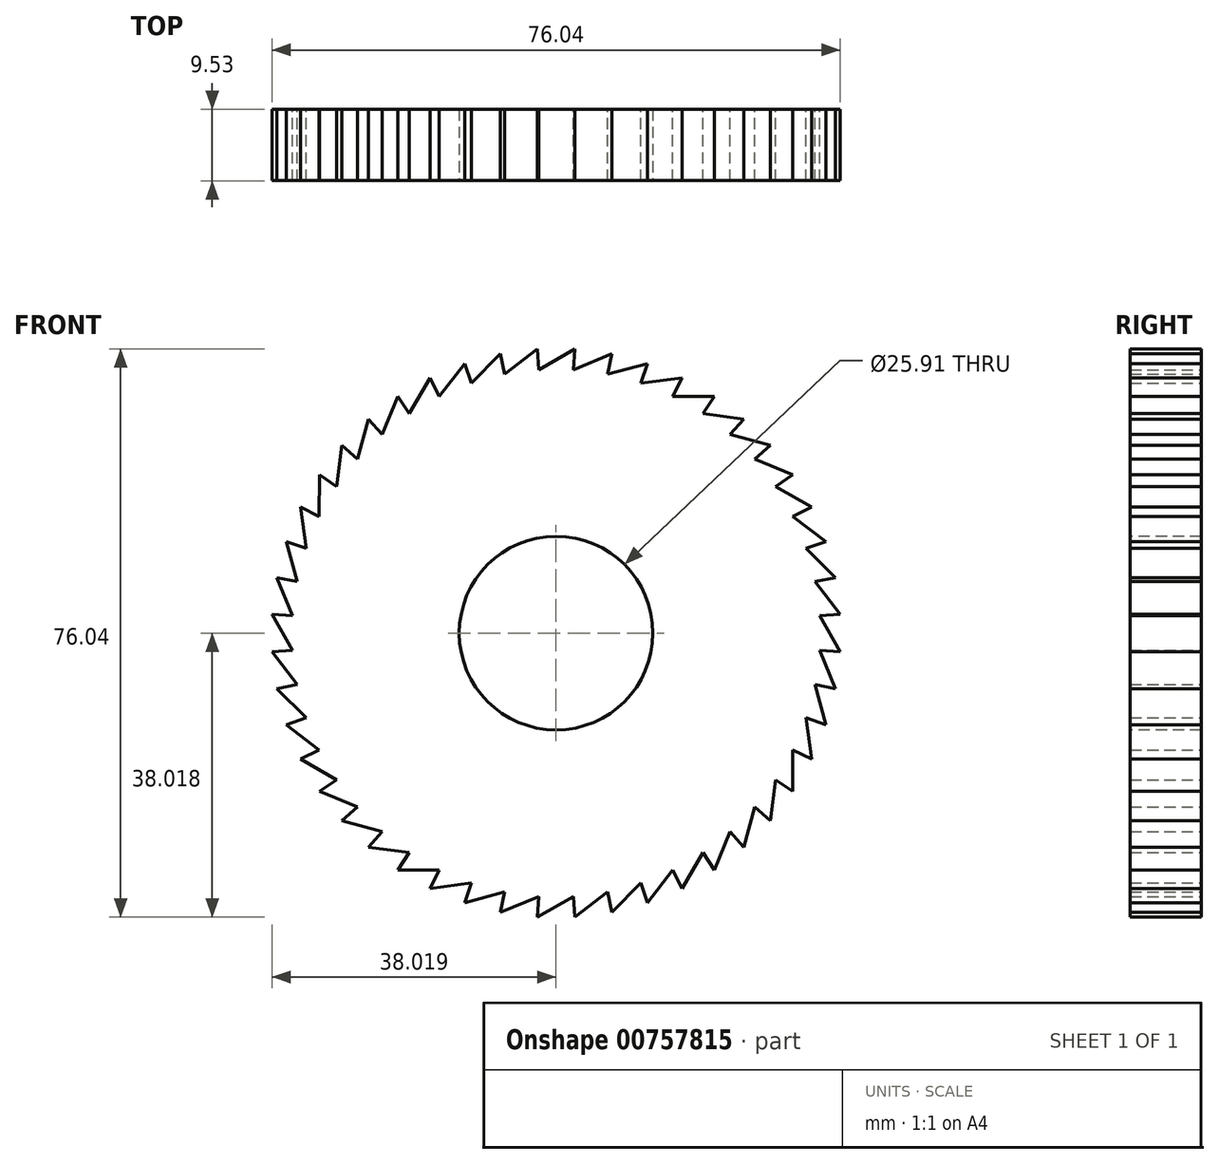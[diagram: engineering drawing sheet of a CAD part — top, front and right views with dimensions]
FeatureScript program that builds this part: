
annotation { "Feature Type Name" : "Feature", "Feature Type Description" : "" }
export const myFeature = defineFeature(function(context is Context, id is Id, definition is map)
    precondition{}
    {
        {
            var Q0;
            Q0=qCreatedBy(makeId("Front.planeOp"),FACE);
            var sketch = newSketch(context, id + "F0", { "sketchPlane" : qUnion([Q0])});
            skLineSegment(sketch, "E0", {"start": v(-136.17, -101.6) * mm, "end": v(-136.17, 101.6) * mm});
            skLineSegment(sketch, "E1", {"start": v(130.53, -101.6) * mm, "end": v(130.53, 101.6) * mm});
            skLineSegment(sketch, "E2", {"start": v(130.53, 101.6) * mm, "end": v(-136.17, 101.6) * mm});
            skLineSegment(sketch, "E3", {"start": v(-136.17, -101.6) * mm, "end": v(130.53, -101.6) * mm});
            skLineSegment(sketch, "E4", {"start": v(130.53, -82.55) * mm, "end": v(13.06, -82.55) * mm});
            skLineSegment(sketch, "E5", {"start": v(13.06, -82.55) * mm, "end": v(13.06, -101.6) * mm});
            skLineSegment(sketch, "E6", {"start": v(13.06, -90.49) * mm, "end": v(130.53, -90.49) * mm});
            skLineSegment(sketch, "E7", {"start": v(13.06, -98.43) * mm, "end": v(68.62, -98.43) * mm});
            skLineSegment(sketch, "E8", {"start": v(68.62, -98.43) * mm, "end": v(68.62, -101.6) * mm});
            skLineSegment(sketch, "E9", {"start": v(68.62, -98.43) * mm, "end": v(68.62, -90.49) * mm});
            skLineSegment(sketch, "E10", {"start": v(68.62, -90.49) * mm, "end": v(68.62, -82.55) * mm});
            skLineSegment(sketch, "E11", {"start": v(-53.64, 28.66) * mm, "end": v(-53.46, 31.43) * mm});
            skLineSegment(sketch, "E12", {"start": v(-48.52, 30.78) * mm, "end": v(-53.64, 28.66) * mm});
            skLineSegment(sketch, "E13", {"start": v(-49.06, 28.05) * mm, "end": v(-48.52, 30.78) * mm});
            skLineSegment(sketch, "E14", {"start": v(-43.7, 29.49) * mm, "end": v(-49.06, 28.05) * mm});
            skLineSegment(sketch, "E15", {"start": v(-44.6, 26.86) * mm, "end": v(-43.7, 29.49) * mm});
            skLineSegment(sketch, "E16", {"start": v(-39.1, 27.58) * mm, "end": v(-44.6, 26.86) * mm});
            skLineSegment(sketch, "E17", {"start": v(-40.33, 25.1) * mm, "end": v(-39.1, 27.58) * mm});
            skLineSegment(sketch, "E18", {"start": v(-34.78, 25.09) * mm, "end": v(-40.33, 25.1) * mm});
            skLineSegment(sketch, "E19", {"start": v(-36.33, 22.78) * mm, "end": v(-34.78, 25.09) * mm});
            skLineSegment(sketch, "E20", {"start": v(-30.83, 22.05) * mm, "end": v(-36.33, 22.78) * mm});
            skLineSegment(sketch, "E21", {"start": v(-32.66, 19.97) * mm, "end": v(-30.83, 22.05) * mm});
            skLineSegment(sketch, "E22", {"start": v(-27.3, 18.53) * mm, "end": v(-32.66, 19.97) * mm});
            skLineSegment(sketch, "E23", {"start": v(-29.4, 16.7) * mm, "end": v(-27.3, 18.53) * mm});
            skLineSegment(sketch, "E24", {"start": v(-24.27, 14.58) * mm, "end": v(-29.4, 16.7) * mm});
            skLineSegment(sketch, "E25", {"start": v(-26.58, 13.03) * mm, "end": v(-24.27, 14.58) * mm});
            skLineSegment(sketch, "E26", {"start": v(-21.78, 10.26) * mm, "end": v(-26.58, 13.03) * mm});
            skLineSegment(sketch, "E27", {"start": v(-24.27, 9.03) * mm, "end": v(-21.78, 10.26) * mm});
            skLineSegment(sketch, "E28", {"start": v(-19.87, 5.66) * mm, "end": v(-24.27, 9.03) * mm});
            skLineSegment(sketch, "E29", {"start": v(-22.5, 4.76) * mm, "end": v(-19.87, 5.66) * mm});
            skLineSegment(sketch, "E30", {"start": v(-18.58, 0.84) * mm, "end": v(-22.5, 4.76) * mm});
            skLineSegment(sketch, "E31", {"start": v(-21.3, 0.3) * mm, "end": v(-18.58, 0.84) * mm});
            skLineSegment(sketch, "E32", {"start": v(-17.93, -4.1) * mm, "end": v(-21.3, 0.3) * mm});
            skLineSegment(sketch, "E33", {"start": v(-20.7, -4.28) * mm, "end": v(-17.93, -4.1) * mm});
            skLineSegment(sketch, "E34", {"start": v(-17.93, -9.08) * mm, "end": v(-20.7, -4.28) * mm});
            skLineSegment(sketch, "E35", {"start": v(-20.7, -8.9) * mm, "end": v(-17.93, -9.08) * mm});
            skLineSegment(sketch, "E36", {"start": v(-18.58, -14.02) * mm, "end": v(-20.7, -8.9) * mm});
            skLineSegment(sketch, "E37", {"start": v(-21.3, -13.48) * mm, "end": v(-18.58, -14.02) * mm});
            skLineSegment(sketch, "E38", {"start": v(-19.87, -18.84) * mm, "end": v(-21.3, -13.48) * mm});
            skLineSegment(sketch, "E39", {"start": v(-22.5, -17.95) * mm, "end": v(-19.87, -18.84) * mm});
            skLineSegment(sketch, "E40", {"start": v(-21.78, -23.44) * mm, "end": v(-22.5, -17.95) * mm});
            skLineSegment(sketch, "E41", {"start": v(-24.27, -22.22) * mm, "end": v(-21.78, -23.44) * mm});
            skLineSegment(sketch, "E42", {"start": v(-24.27, -27.76) * mm, "end": v(-24.27, -22.22) * mm});
            skLineSegment(sketch, "E43", {"start": v(-26.58, -26.22) * mm, "end": v(-24.27, -27.76) * mm});
            skLineSegment(sketch, "E44", {"start": v(-27.3, -31.71) * mm, "end": v(-26.58, -26.22) * mm});
            skLineSegment(sketch, "E45", {"start": v(-29.4, -29.88) * mm, "end": v(-27.3, -31.71) * mm});
            skLineSegment(sketch, "E46", {"start": v(-30.83, -35.24) * mm, "end": v(-29.4, -29.88) * mm});
            skLineSegment(sketch, "E47", {"start": v(-32.66, -33.15) * mm, "end": v(-30.83, -35.24) * mm});
            skLineSegment(sketch, "E48", {"start": v(-34.78, -38.27) * mm, "end": v(-32.66, -33.15) * mm});
            skLineSegment(sketch, "E49", {"start": v(-36.33, -35.96) * mm, "end": v(-34.78, -38.27) * mm});
            skLineSegment(sketch, "E50", {"start": v(-39.1, -40.76) * mm, "end": v(-36.33, -35.96) * mm});
            skLineSegment(sketch, "E51", {"start": v(-40.33, -38.27) * mm, "end": v(-39.1, -40.76) * mm});
            skLineSegment(sketch, "E52", {"start": v(-43.7, -42.67) * mm, "end": v(-40.33, -38.27) * mm});
            skLineSegment(sketch, "E53", {"start": v(-44.6, -40.04) * mm, "end": v(-43.7, -42.67) * mm});
            skLineSegment(sketch, "E54", {"start": v(-48.52, -43.96) * mm, "end": v(-44.6, -40.04) * mm});
            skLineSegment(sketch, "E55", {"start": v(-49.06, -41.24) * mm, "end": v(-48.52, -43.96) * mm});
            skLineSegment(sketch, "E56", {"start": v(-53.46, -44.61) * mm, "end": v(-49.06, -41.24) * mm});
            skLineSegment(sketch, "E57", {"start": v(-53.64, -41.84) * mm, "end": v(-53.46, -44.61) * mm});
            skLineSegment(sketch, "E58", {"start": v(-58.44, -44.61) * mm, "end": v(-53.64, -41.84) * mm});
            skLineSegment(sketch, "E59", {"start": v(-58.26, -41.84) * mm, "end": v(-58.44, -44.61) * mm});
            skLineSegment(sketch, "E60", {"start": v(-63.38, -43.96) * mm, "end": v(-58.26, -41.84) * mm});
            skLineSegment(sketch, "E61", {"start": v(-68.2, -42.67) * mm, "end": v(-62.84, -41.24) * mm});
            skLineSegment(sketch, "E62", {"start": v(-67.3, -40.04) * mm, "end": v(-68.2, -42.67) * mm});
            skLineSegment(sketch, "E63", {"start": v(-72.8, -40.76) * mm, "end": v(-67.3, -40.04) * mm});
            skLineSegment(sketch, "E64", {"start": v(-71.57, -38.27) * mm, "end": v(-72.8, -40.76) * mm});
            skLineSegment(sketch, "E65", {"start": v(-77.12, -38.27) * mm, "end": v(-71.57, -38.27) * mm});
            skLineSegment(sketch, "E66", {"start": v(-75.58, -35.96) * mm, "end": v(-77.12, -38.27) * mm});
            skLineSegment(sketch, "E67", {"start": v(-81.07, -35.24) * mm, "end": v(-75.58, -35.96) * mm});
            skLineSegment(sketch, "E68", {"start": v(-79.24, -33.15) * mm, "end": v(-81.07, -35.24) * mm});
            skLineSegment(sketch, "E69", {"start": v(-84.6, -31.71) * mm, "end": v(-79.24, -33.15) * mm});
            skLineSegment(sketch, "E70", {"start": v(-82.5, -29.88) * mm, "end": v(-84.6, -31.71) * mm});
            skLineSegment(sketch, "E71", {"start": v(-87.63, -27.76) * mm, "end": v(-82.5, -29.88) * mm});
            skLineSegment(sketch, "E72", {"start": v(-85.32, -26.22) * mm, "end": v(-87.63, -27.76) * mm});
            skLineSegment(sketch, "E73", {"start": v(-90.12, -23.44) * mm, "end": v(-85.32, -26.22) * mm});
            skLineSegment(sketch, "E74", {"start": v(-87.63, -22.22) * mm, "end": v(-90.12, -23.44) * mm});
            skLineSegment(sketch, "E75", {"start": v(-92.03, -18.84) * mm, "end": v(-87.63, -22.22) * mm});
            skLineSegment(sketch, "E76", {"start": v(-89.4, -17.95) * mm, "end": v(-92.03, -18.84) * mm});
            skLineSegment(sketch, "E77", {"start": v(-93.32, -14.02) * mm, "end": v(-89.4, -17.95) * mm});
            skLineSegment(sketch, "E78", {"start": v(-90.6, -13.48) * mm, "end": v(-93.32, -14.02) * mm});
            skLineSegment(sketch, "E79", {"start": v(-93.97, -9.08) * mm, "end": v(-90.6, -13.48) * mm});
            skLineSegment(sketch, "E80", {"start": v(-91.2, -8.9) * mm, "end": v(-93.97, -9.08) * mm});
            skLineSegment(sketch, "E81", {"start": v(-93.97, -4.1) * mm, "end": v(-91.2, -8.9) * mm});
            skLineSegment(sketch, "E82", {"start": v(-91.2, -4.28) * mm, "end": v(-93.97, -4.1) * mm});
            skLineSegment(sketch, "E83", {"start": v(-93.32, 0.84) * mm, "end": v(-91.2, -4.28) * mm});
            skLineSegment(sketch, "E84", {"start": v(-90.6, 0.3) * mm, "end": v(-93.32, 0.84) * mm});
            skLineSegment(sketch, "E85", {"start": v(-92.03, 5.66) * mm, "end": v(-90.6, 0.3) * mm});
            skLineSegment(sketch, "E86", {"start": v(-89.4, 4.76) * mm, "end": v(-92.03, 5.66) * mm});
            skLineSegment(sketch, "E87", {"start": v(-90.12, 10.26) * mm, "end": v(-89.4, 4.76) * mm});
            skLineSegment(sketch, "E88", {"start": v(-87.63, 9.03) * mm, "end": v(-90.12, 10.26) * mm});
            skLineSegment(sketch, "E89", {"start": v(-87.63, 14.58) * mm, "end": v(-87.63, 9.03) * mm});
            skLineSegment(sketch, "E90", {"start": v(-85.32, 13.03) * mm, "end": v(-87.63, 14.58) * mm});
            skLineSegment(sketch, "E91", {"start": v(-84.6, 18.53) * mm, "end": v(-85.32, 13.03) * mm});
            skLineSegment(sketch, "E92", {"start": v(-82.5, 16.7) * mm, "end": v(-84.6, 18.53) * mm});
            skLineSegment(sketch, "E93", {"start": v(-81.07, 22.05) * mm, "end": v(-82.5, 16.7) * mm});
            skLineSegment(sketch, "E94", {"start": v(-79.24, 19.97) * mm, "end": v(-81.07, 22.05) * mm});
            skLineSegment(sketch, "E95", {"start": v(-77.12, 25.09) * mm, "end": v(-79.24, 19.97) * mm});
            skLineSegment(sketch, "E96", {"start": v(-75.58, 22.78) * mm, "end": v(-77.12, 25.09) * mm});
            skLineSegment(sketch, "E97", {"start": v(-72.8, 27.58) * mm, "end": v(-75.58, 22.78) * mm});
            skLineSegment(sketch, "E98", {"start": v(-71.57, 25.1) * mm, "end": v(-72.8, 27.58) * mm});
            skLineSegment(sketch, "E99", {"start": v(-68.2, 29.49) * mm, "end": v(-71.57, 25.1) * mm});
            skLineSegment(sketch, "E100", {"start": v(-67.3, 26.86) * mm, "end": v(-68.2, 29.49) * mm});
            skLineSegment(sketch, "E101", {"start": v(-63.38, 30.78) * mm, "end": v(-67.3, 26.86) * mm});
            skLineSegment(sketch, "E102", {"start": v(-62.84, 28.05) * mm, "end": v(-63.38, 30.78) * mm});
            skLineSegment(sketch, "E103", {"start": v(-58.44, 31.43) * mm, "end": v(-62.84, 28.05) * mm});
            skLineSegment(sketch, "E104", {"start": v(-58.26, 28.66) * mm, "end": v(-58.44, 31.43) * mm});
            skLineSegment(sketch, "E105", {"start": v(-53.46, 31.43) * mm, "end": v(-58.26, 28.66) * mm});
            skCircle(sketch, "E106", {"center": v(-55.95, -6.6) * mm, "radius": 8.9 * mm});
            skLineSegment(sketch, "E107", {"start": v(-62.84, -41.24) * mm, "end": v(-63.38, -43.96) * mm});
            skCircle(sketch, "E108", {"center": v(-55.95, -6.6) * mm, "radius": 8.73 * mm});
            skLineSegment(sketch, "E109", {"start": v(-46.26, 37.72) * mm, "end": v(-19.3, 38.64) * mm});
            skLineSegment(sketch, "E110", {"start": v(-52.38, 30.8) * mm, "end": v(-52.4, 31.16) * mm});
            skLineSegment(sketch, "E111", {"start": v(-52.38, 30.8) * mm, "end": v(-51.42, 30.84) * mm});
            skLineSegment(sketch, "E112", {"start": v(-40.64, 31.2) * mm, "end": v(-19.77, 25.99) * mm});
            skArc(sketch, "E113", {"start": v(-46.26, 37.72) * mm, "mid": v(-50.69, 35.71) * mm, "end": v(-52.4, 31.16) * mm});
            skArc(sketch, "E114", {"start": v(-40.64, 31.2) * mm, "mid": v(-46.11, 33.48) * mm, "end": v(-51.42, 30.84) * mm});
            skArc(sketch, "E115", {"start": v(-19.77, 25.99) * mm, "mid": v(-12.73, 32.06) * mm, "end": v(-19.3, 38.64) * mm});
            skCircle(sketch, "E116", {"center": v(-19.07, 32.3) * mm, "radius": 3.19 * mm});
            skLineSegment(sketch, "E117", {"start": v(58.58, 2.14) * mm, "end": v(67.76, 2.14) * mm});
            skLineSegment(sketch, "E118", {"start": v(67.76, 2.14) * mm, "end": v(67.93, 2.31) * mm});
            skLineSegment(sketch, "E119", {"start": v(58.58, 2.14) * mm, "end": v(58.4, 2.31) * mm});
            skLineSegment(sketch, "E120", {"start": v(58.4, -15.5) * mm, "end": v(58.58, -15.32) * mm});
            skLineSegment(sketch, "E121", {"start": v(58.58, -15.32) * mm, "end": v(67.76, -15.32) * mm});
            skLineSegment(sketch, "E122", {"start": v(67.76, -15.32) * mm, "end": v(67.93, -15.5) * mm});
            skLineSegment(sketch, "E123", {"start": v(67.93, -4.28) * mm, "end": v(58.4, -4.28) * mm});
            skLineSegment(sketch, "E124", {"start": v(58.4, -9.08) * mm, "end": v(58.4, -4.28) * mm});
            skLineSegment(sketch, "E125", {"start": v(67.93, -9.08) * mm, "end": v(58.4, -9.08) * mm});
            skLineSegment(sketch, "E126", {"start": v(67.93, -9.08) * mm, "end": v(67.93, -4.28) * mm});
            skLineSegment(sketch, "E127", {"start": v(67.93, -4.1) * mm, "end": v(58.4, -4.1) * mm});
            skLineSegment(sketch, "E128", {"start": v(58.4, -4.28) * mm, "end": v(58.4, -4.1) * mm});
            skLineSegment(sketch, "E129", {"start": v(67.93, -4.28) * mm, "end": v(67.93, -4.1) * mm});
            skLineSegment(sketch, "E130", {"start": v(67.93, 0.3) * mm, "end": v(58.4, 0.3) * mm});
            skLineSegment(sketch, "E131", {"start": v(58.4, -4.1) * mm, "end": v(58.4, 0.3) * mm});
            skLineSegment(sketch, "E132", {"start": v(67.93, -4.1) * mm, "end": v(67.93, 0.3) * mm});
            skLineSegment(sketch, "E133", {"start": v(67.93, -14.02) * mm, "end": v(58.4, -14.02) * mm});
            skLineSegment(sketch, "E134", {"start": v(58.4, -14.02) * mm, "end": v(58.4, -9.08) * mm});
            skLineSegment(sketch, "E135", {"start": v(67.93, -14.02) * mm, "end": v(67.93, -9.08) * mm});
            skLineSegment(sketch, "E136", {"start": v(67.93, 4.76) * mm, "end": v(58.4, 4.76) * mm});
            skLineSegment(sketch, "E137", {"start": v(67.93, 0.84) * mm, "end": v(58.4, 0.84) * mm});
            skLineSegment(sketch, "E138", {"start": v(58.4, 0.84) * mm, "end": v(58.4, 4.76) * mm});
            skLineSegment(sketch, "E139", {"start": v(67.93, 0.84) * mm, "end": v(67.93, 4.76) * mm});
            skLineSegment(sketch, "E140", {"start": v(58.4, 0.3) * mm, "end": v(58.4, 0.84) * mm});
            skLineSegment(sketch, "E141", {"start": v(67.93, 0.3) * mm, "end": v(67.93, 0.84) * mm});
            skLineSegment(sketch, "E142", {"start": v(67.93, -18.84) * mm, "end": v(58.4, -18.84) * mm});
            skLineSegment(sketch, "E143", {"start": v(58.4, -18.84) * mm, "end": v(58.4, -14.02) * mm});
            skLineSegment(sketch, "E144", {"start": v(67.93, -18.84) * mm, "end": v(67.93, -14.02) * mm});
            skLineSegment(sketch, "E145", {"start": v(67.93, 9.03) * mm, "end": v(58.4, 9.03) * mm});
            skLineSegment(sketch, "E146", {"start": v(67.93, 5.66) * mm, "end": v(58.4, 5.66) * mm});
            skLineSegment(sketch, "E147", {"start": v(58.4, 5.66) * mm, "end": v(58.4, 9.03) * mm});
            skLineSegment(sketch, "E148", {"start": v(67.93, 5.66) * mm, "end": v(67.93, 9.03) * mm});
            skLineSegment(sketch, "E149", {"start": v(58.4, 4.76) * mm, "end": v(58.4, 5.66) * mm});
            skLineSegment(sketch, "E150", {"start": v(67.93, 4.76) * mm, "end": v(67.93, 5.66) * mm});
            skLineSegment(sketch, "E151", {"start": v(67.93, -23.44) * mm, "end": v(58.4, -23.44) * mm});
            skLineSegment(sketch, "E152", {"start": v(58.4, -23.44) * mm, "end": v(58.4, -18.84) * mm});
            skLineSegment(sketch, "E153", {"start": v(67.93, -23.44) * mm, "end": v(67.93, -18.84) * mm});
            skLineSegment(sketch, "E154", {"start": v(67.93, 10.26) * mm, "end": v(58.4, 10.26) * mm});
            skLineSegment(sketch, "E155", {"start": v(58.4, 9.03) * mm, "end": v(58.4, 10.26) * mm});
            skLineSegment(sketch, "E156", {"start": v(67.93, 9.03) * mm, "end": v(67.93, 10.26) * mm});
            skLineSegment(sketch, "E157", {"start": v(67.93, 13.03) * mm, "end": v(58.4, 13.03) * mm});
            skLineSegment(sketch, "E158", {"start": v(58.4, 10.26) * mm, "end": v(58.4, 13.03) * mm});
            skLineSegment(sketch, "E159", {"start": v(67.93, 10.26) * mm, "end": v(67.93, 13.03) * mm});
            skLineSegment(sketch, "E160", {"start": v(67.93, -27.76) * mm, "end": v(58.4, -27.76) * mm});
            skLineSegment(sketch, "E161", {"start": v(58.4, -27.76) * mm, "end": v(58.4, -23.44) * mm});
            skLineSegment(sketch, "E162", {"start": v(67.93, -27.76) * mm, "end": v(67.93, -23.44) * mm});
            skLineSegment(sketch, "E163", {"start": v(67.93, 16.7) * mm, "end": v(58.4, 16.7) * mm});
            skLineSegment(sketch, "E164", {"start": v(67.93, 14.58) * mm, "end": v(58.4, 14.58) * mm});
            skLineSegment(sketch, "E165", {"start": v(58.4, 14.58) * mm, "end": v(58.4, 16.7) * mm});
            skLineSegment(sketch, "E166", {"start": v(67.93, 14.58) * mm, "end": v(67.93, 16.7) * mm});
            skLineSegment(sketch, "E167", {"start": v(58.4, 13.03) * mm, "end": v(58.4, 14.58) * mm});
            skLineSegment(sketch, "E168", {"start": v(67.93, 13.03) * mm, "end": v(67.93, 14.58) * mm});
            skLineSegment(sketch, "E169", {"start": v(67.93, -31.71) * mm, "end": v(58.4, -31.71) * mm});
            skLineSegment(sketch, "E170", {"start": v(58.4, -31.71) * mm, "end": v(58.4, -27.76) * mm});
            skLineSegment(sketch, "E171", {"start": v(67.93, -31.71) * mm, "end": v(67.93, -27.76) * mm});
            skLineSegment(sketch, "E172", {"start": v(67.93, 19.97) * mm, "end": v(58.4, 19.97) * mm});
            skLineSegment(sketch, "E173", {"start": v(67.93, 18.53) * mm, "end": v(58.4, 18.53) * mm});
            skLineSegment(sketch, "E174", {"start": v(58.4, 18.53) * mm, "end": v(58.4, 19.97) * mm});
            skLineSegment(sketch, "E175", {"start": v(67.93, 18.53) * mm, "end": v(67.93, 19.97) * mm});
            skLineSegment(sketch, "E176", {"start": v(58.4, 16.7) * mm, "end": v(58.4, 18.53) * mm});
            skLineSegment(sketch, "E177", {"start": v(67.93, 16.7) * mm, "end": v(67.93, 18.53) * mm});
            skLineSegment(sketch, "E178", {"start": v(67.93, -35.24) * mm, "end": v(58.4, -35.24) * mm});
            skLineSegment(sketch, "E179", {"start": v(58.4, -35.24) * mm, "end": v(58.4, -31.71) * mm});
            skLineSegment(sketch, "E180", {"start": v(67.93, -35.24) * mm, "end": v(67.93, -31.71) * mm});
            skLineSegment(sketch, "E181", {"start": v(67.93, 22.78) * mm, "end": v(58.4, 22.78) * mm});
            skLineSegment(sketch, "E182", {"start": v(67.93, 22.05) * mm, "end": v(58.4, 22.05) * mm});
            skLineSegment(sketch, "E183", {"start": v(58.4, 22.05) * mm, "end": v(58.4, 22.78) * mm});
            skLineSegment(sketch, "E184", {"start": v(67.93, 22.05) * mm, "end": v(67.93, 22.78) * mm});
            skLineSegment(sketch, "E185", {"start": v(58.4, 19.97) * mm, "end": v(58.4, 22.05) * mm});
            skLineSegment(sketch, "E186", {"start": v(67.93, 19.97) * mm, "end": v(67.93, 22.05) * mm});
            skLineSegment(sketch, "E187", {"start": v(67.93, -38.27) * mm, "end": v(58.4, -38.27) * mm});
            skLineSegment(sketch, "E188", {"start": v(58.4, -38.27) * mm, "end": v(58.4, -35.24) * mm});
            skLineSegment(sketch, "E189", {"start": v(67.93, -38.27) * mm, "end": v(67.93, -35.24) * mm});
            skLineSegment(sketch, "E190", {"start": v(67.93, 25.1) * mm, "end": v(58.4, 25.1) * mm});
            skLineSegment(sketch, "E191", {"start": v(67.93, 25.09) * mm, "end": v(58.4, 25.09) * mm});
            skLineSegment(sketch, "E192", {"start": v(58.4, 25.09) * mm, "end": v(58.4, 25.1) * mm});
            skLineSegment(sketch, "E193", {"start": v(67.93, 25.09) * mm, "end": v(67.93, 25.1) * mm});
            skLineSegment(sketch, "E194", {"start": v(58.4, 22.78) * mm, "end": v(58.4, 25.09) * mm});
            skLineSegment(sketch, "E195", {"start": v(67.93, 22.78) * mm, "end": v(67.93, 25.09) * mm});
            skLineSegment(sketch, "E196", {"start": v(67.93, -40.76) * mm, "end": v(58.4, -40.76) * mm});
            skLineSegment(sketch, "E197", {"start": v(58.4, -40.76) * mm, "end": v(58.4, -38.27) * mm});
            skLineSegment(sketch, "E198", {"start": v(67.93, -40.76) * mm, "end": v(67.93, -38.27) * mm});
            skLineSegment(sketch, "E199", {"start": v(67.93, 27.58) * mm, "end": v(58.4, 27.58) * mm});
            skLineSegment(sketch, "E200", {"start": v(58.4, 25.1) * mm, "end": v(58.4, 27.58) * mm});
            skLineSegment(sketch, "E201", {"start": v(67.93, 25.1) * mm, "end": v(67.93, 27.58) * mm});
            skLineSegment(sketch, "E202", {"start": v(67.93, -42.67) * mm, "end": v(58.4, -42.67) * mm});
            skLineSegment(sketch, "E203", {"start": v(58.4, -42.67) * mm, "end": v(58.4, -40.76) * mm});
            skLineSegment(sketch, "E204", {"start": v(67.93, -42.67) * mm, "end": v(67.93, -40.76) * mm});
            skLineSegment(sketch, "E205", {"start": v(67.93, 29.49) * mm, "end": v(58.4, 29.49) * mm});
            skLineSegment(sketch, "E206", {"start": v(58.4, 27.58) * mm, "end": v(58.4, 29.49) * mm});
            skLineSegment(sketch, "E207", {"start": v(67.93, 27.58) * mm, "end": v(67.93, 29.49) * mm});
            skLineSegment(sketch, "E208", {"start": v(67.93, -43.96) * mm, "end": v(58.4, -43.96) * mm});
            skLineSegment(sketch, "E209", {"start": v(58.4, -43.96) * mm, "end": v(58.4, -42.67) * mm});
            skLineSegment(sketch, "E210", {"start": v(67.93, -43.96) * mm, "end": v(67.93, -42.67) * mm});
            skLineSegment(sketch, "E211", {"start": v(67.93, 30.78) * mm, "end": v(58.4, 30.78) * mm});
            skLineSegment(sketch, "E212", {"start": v(58.4, 29.49) * mm, "end": v(58.4, 30.78) * mm});
            skLineSegment(sketch, "E213", {"start": v(67.93, 29.49) * mm, "end": v(67.93, 30.78) * mm});
            skLineSegment(sketch, "E214", {"start": v(67.93, -44.61) * mm, "end": v(58.4, -44.61) * mm});
            skLineSegment(sketch, "E215", {"start": v(58.4, -44.61) * mm, "end": v(58.4, -43.96) * mm});
            skLineSegment(sketch, "E216", {"start": v(67.93, -44.61) * mm, "end": v(67.93, -43.96) * mm});
            skLineSegment(sketch, "E217", {"start": v(67.93, 31.43) * mm, "end": v(58.4, 31.43) * mm});
            skLineSegment(sketch, "E218", {"start": v(58.4, 30.78) * mm, "end": v(58.4, 31.43) * mm});
            skLineSegment(sketch, "E219", {"start": v(67.93, 30.78) * mm, "end": v(67.93, 31.43) * mm});
            skLineSegment(sketch, "E220", {"start": v(104.22, 94.72) * mm, "end": v(104.29, 96.04) * mm});
            skLineSegment(sketch, "E221", {"start": v(106.03, 95.26) * mm, "end": v(104.22, 94.72) * mm});
            skLineSegment(sketch, "E222", {"start": v(105.84, 94) * mm, "end": v(106.03, 95.26) * mm});
            skLineSegment(sketch, "E223", {"start": v(107.73, 94.18) * mm, "end": v(105.84, 94) * mm});
            skLineSegment(sketch, "E224", {"start": v(107.42, 93) * mm, "end": v(107.73, 94.18) * mm});
            skLineSegment(sketch, "E225", {"start": v(109.36, 92.83) * mm, "end": v(107.42, 93) * mm});
            skLineSegment(sketch, "E226", {"start": v(108.93, 91.74) * mm, "end": v(109.36, 92.83) * mm});
            skLineSegment(sketch, "E227", {"start": v(110.89, 91.22) * mm, "end": v(108.93, 91.74) * mm});
            skLineSegment(sketch, "E228", {"start": v(110.34, 90.25) * mm, "end": v(110.89, 91.22) * mm});
            skLineSegment(sketch, "E229", {"start": v(112.29, 89.38) * mm, "end": v(110.34, 90.25) * mm});
            skLineSegment(sketch, "E230", {"start": v(111.64, 88.55) * mm, "end": v(112.29, 89.38) * mm});
            skLineSegment(sketch, "E231", {"start": v(113.53, 87.35) * mm, "end": v(111.64, 88.55) * mm});
            skLineSegment(sketch, "E232", {"start": v(112.8, 86.67) * mm, "end": v(113.53, 87.35) * mm});
            skLineSegment(sketch, "E233", {"start": v(114.6, 85.16) * mm, "end": v(112.8, 86.67) * mm});
            skLineSegment(sketch, "E234", {"start": v(113.79, 84.63) * mm, "end": v(114.6, 85.16) * mm});
            skLineSegment(sketch, "E235", {"start": v(115.49, 82.84) * mm, "end": v(113.79, 84.63) * mm});
            skLineSegment(sketch, "E236", {"start": v(114.6, 82.49) * mm, "end": v(115.49, 82.84) * mm});
            skLineSegment(sketch, "E237", {"start": v(116.16, 80.44) * mm, "end": v(114.6, 82.49) * mm});
            skLineSegment(sketch, "E238", {"start": v(115.23, 80.26) * mm, "end": v(116.16, 80.44) * mm});
            skLineSegment(sketch, "E239", {"start": v(116.62, 78) * mm, "end": v(115.23, 80.26) * mm});
            skLineSegment(sketch, "E240", {"start": v(115.65, 78) * mm, "end": v(116.62, 78) * mm});
            skLineSegment(sketch, "E241", {"start": v(116.85, 75.56) * mm, "end": v(115.65, 78) * mm});
            skLineSegment(sketch, "E242", {"start": v(115.87, 75.74) * mm, "end": v(116.85, 75.56) * mm});
            skLineSegment(sketch, "E243", {"start": v(116.85, 73.16) * mm, "end": v(115.87, 75.74) * mm});
            skLineSegment(sketch, "E244", {"start": v(115.87, 73.5) * mm, "end": v(116.85, 73.16) * mm});
            skLineSegment(sketch, "E245", {"start": v(116.62, 70.84) * mm, "end": v(115.87, 73.5) * mm});
            skLineSegment(sketch, "E246", {"start": v(115.65, 71.36) * mm, "end": v(116.62, 70.84) * mm});
            skLineSegment(sketch, "E247", {"start": v(116.16, 68.64) * mm, "end": v(115.65, 71.36) * mm});
            skLineSegment(sketch, "E248", {"start": v(115.23, 69.32) * mm, "end": v(116.16, 68.64) * mm});
            skLineSegment(sketch, "E249", {"start": v(115.49, 66.6) * mm, "end": v(115.23, 69.32) * mm});
            skLineSegment(sketch, "E250", {"start": v(114.6, 67.43) * mm, "end": v(115.49, 66.6) * mm});
            skLineSegment(sketch, "E251", {"start": v(114.6, 64.76) * mm, "end": v(114.6, 67.43) * mm});
            skLineSegment(sketch, "E252", {"start": v(113.79, 65.73) * mm, "end": v(114.6, 64.76) * mm});
            skLineSegment(sketch, "E253", {"start": v(113.53, 63.15) * mm, "end": v(113.79, 65.73) * mm});
            skLineSegment(sketch, "E254", {"start": v(112.8, 64.23) * mm, "end": v(113.53, 63.15) * mm});
            skLineSegment(sketch, "E255", {"start": v(112.29, 61.78) * mm, "end": v(112.8, 64.23) * mm});
            skLineSegment(sketch, "E256", {"start": v(111.64, 62.96) * mm, "end": v(112.29, 61.78) * mm});
            skLineSegment(sketch, "E257", {"start": v(110.89, 60.7) * mm, "end": v(111.64, 62.96) * mm});
            skLineSegment(sketch, "E258", {"start": v(110.34, 61.95) * mm, "end": v(110.89, 60.7) * mm});
            skLineSegment(sketch, "E259", {"start": v(109.36, 59.9) * mm, "end": v(110.34, 61.95) * mm});
            skLineSegment(sketch, "E260", {"start": v(108.93, 61.22) * mm, "end": v(109.36, 59.9) * mm});
            skLineSegment(sketch, "E261", {"start": v(107.73, 59.42) * mm, "end": v(108.93, 61.22) * mm});
            skLineSegment(sketch, "E262", {"start": v(107.42, 60.77) * mm, "end": v(107.73, 59.42) * mm});
            skLineSegment(sketch, "E263", {"start": v(106.03, 59.26) * mm, "end": v(107.42, 60.77) * mm});
            skLineSegment(sketch, "E264", {"start": v(105.84, 60.62) * mm, "end": v(106.03, 59.26) * mm});
            skLineSegment(sketch, "E265", {"start": v(104.29, 59.41) * mm, "end": v(105.84, 60.62) * mm});
            skLineSegment(sketch, "E266", {"start": v(104.22, 60.76) * mm, "end": v(104.29, 59.41) * mm});
            skLineSegment(sketch, "E267", {"start": v(102.52, 59.88) * mm, "end": v(104.22, 60.76) * mm});
            skLineSegment(sketch, "E268", {"start": v(102.59, 61.2) * mm, "end": v(102.52, 59.88) * mm});
            skLineSegment(sketch, "E269", {"start": v(100.78, 60.66) * mm, "end": v(102.59, 61.2) * mm});
            skLineSegment(sketch, "E270", {"start": v(100.97, 61.92) * mm, "end": v(100.78, 60.66) * mm});
            skLineSegment(sketch, "E271", {"start": v(99.07, 61.74) * mm, "end": v(100.97, 61.92) * mm});
            skLineSegment(sketch, "E272", {"start": v(99.4, 62.92) * mm, "end": v(99.07, 61.74) * mm});
            skLineSegment(sketch, "E273", {"start": v(97.45, 63.1) * mm, "end": v(99.4, 62.92) * mm});
            skLineSegment(sketch, "E274", {"start": v(97.88, 64.18) * mm, "end": v(97.45, 63.1) * mm});
            skLineSegment(sketch, "E275", {"start": v(95.92, 64.7) * mm, "end": v(97.88, 64.18) * mm});
            skLineSegment(sketch, "E276", {"start": v(96.47, 65.67) * mm, "end": v(95.92, 64.7) * mm});
            skLineSegment(sketch, "E277", {"start": v(94.52, 66.54) * mm, "end": v(96.47, 65.67) * mm});
            skLineSegment(sketch, "E278", {"start": v(95.17, 67.37) * mm, "end": v(94.52, 66.54) * mm});
            skLineSegment(sketch, "E279", {"start": v(93.28, 68.57) * mm, "end": v(95.17, 67.37) * mm});
            skLineSegment(sketch, "E280", {"start": v(94.01, 69.26) * mm, "end": v(93.28, 68.57) * mm});
            skLineSegment(sketch, "E281", {"start": v(92.2, 70.77) * mm, "end": v(94.01, 69.26) * mm});
            skLineSegment(sketch, "E282", {"start": v(93.02, 71.29) * mm, "end": v(92.2, 70.77) * mm});
            skLineSegment(sketch, "E283", {"start": v(91.32, 73.08) * mm, "end": v(93.02, 71.29) * mm});
            skLineSegment(sketch, "E284", {"start": v(92.2, 73.44) * mm, "end": v(91.32, 73.08) * mm});
            skLineSegment(sketch, "E285", {"start": v(90.65, 75.48) * mm, "end": v(92.2, 73.44) * mm});
            skLineSegment(sketch, "E286", {"start": v(91.58, 75.66) * mm, "end": v(90.65, 75.48) * mm});
            skLineSegment(sketch, "E287", {"start": v(90.2, 77.92) * mm, "end": v(91.58, 75.66) * mm});
            skLineSegment(sketch, "E288", {"start": v(91.16, 77.92) * mm, "end": v(90.2, 77.92) * mm});
            skLineSegment(sketch, "E289", {"start": v(89.96, 80.36) * mm, "end": v(91.16, 77.92) * mm});
            skLineSegment(sketch, "E290", {"start": v(90.94, 80.19) * mm, "end": v(89.96, 80.36) * mm});
            skLineSegment(sketch, "E291", {"start": v(89.96, 82.76) * mm, "end": v(90.94, 80.19) * mm});
            skLineSegment(sketch, "E292", {"start": v(90.94, 82.41) * mm, "end": v(89.96, 82.76) * mm});
            skLineSegment(sketch, "E293", {"start": v(90.2, 85.08) * mm, "end": v(90.94, 82.41) * mm});
            skLineSegment(sketch, "E294", {"start": v(91.16, 84.56) * mm, "end": v(90.2, 85.08) * mm});
            skLineSegment(sketch, "E295", {"start": v(90.65, 87.28) * mm, "end": v(91.16, 84.56) * mm});
            skLineSegment(sketch, "E296", {"start": v(91.58, 86.6) * mm, "end": v(90.65, 87.28) * mm});
            skLineSegment(sketch, "E297", {"start": v(91.32, 89.32) * mm, "end": v(91.58, 86.6) * mm});
            skLineSegment(sketch, "E298", {"start": v(92.2, 88.49) * mm, "end": v(91.32, 89.32) * mm});
            skLineSegment(sketch, "E299", {"start": v(92.2, 91.16) * mm, "end": v(92.2, 88.49) * mm});
            skLineSegment(sketch, "E300", {"start": v(93.02, 90.2) * mm, "end": v(92.2, 91.16) * mm});
            skLineSegment(sketch, "E301", {"start": v(93.28, 92.78) * mm, "end": v(93.02, 90.2) * mm});
            skLineSegment(sketch, "E302", {"start": v(94.01, 91.7) * mm, "end": v(93.28, 92.78) * mm});
            skLineSegment(sketch, "E303", {"start": v(94.52, 94.14) * mm, "end": v(94.01, 91.7) * mm});
            skLineSegment(sketch, "E304", {"start": v(95.17, 92.96) * mm, "end": v(94.52, 94.14) * mm});
            skLineSegment(sketch, "E305", {"start": v(95.92, 95.23) * mm, "end": v(95.17, 92.96) * mm});
            skLineSegment(sketch, "E306", {"start": v(96.47, 93.97) * mm, "end": v(95.92, 95.23) * mm});
            skLineSegment(sketch, "E307", {"start": v(97.45, 96.02) * mm, "end": v(96.47, 93.97) * mm});
            skLineSegment(sketch, "E308", {"start": v(97.88, 94.7) * mm, "end": v(97.45, 96.02) * mm});
            skLineSegment(sketch, "E309", {"start": v(99.07, 96.5) * mm, "end": v(97.88, 94.7) * mm});
            skLineSegment(sketch, "E310", {"start": v(99.4, 95.15) * mm, "end": v(99.07, 96.5) * mm});
            skLineSegment(sketch, "E311", {"start": v(100.78, 96.67) * mm, "end": v(99.4, 95.15) * mm});
            skLineSegment(sketch, "E312", {"start": v(100.97, 95.3) * mm, "end": v(100.78, 96.67) * mm});
            skLineSegment(sketch, "E313", {"start": v(102.52, 96.51) * mm, "end": v(100.97, 95.3) * mm});
            skLineSegment(sketch, "E314", {"start": v(102.59, 95.16) * mm, "end": v(102.52, 96.51) * mm});
            skLineSegment(sketch, "E315", {"start": v(104.29, 96.04) * mm, "end": v(102.59, 95.16) * mm});
            skLineSegment(sketch, "E316", {"start": v(106.55, 77.12) * mm, "end": v(106.55, 77) * mm});
            skLineSegment(sketch, "E317", {"start": v(106.55, 77) * mm, "end": v(106.55, 76.9) * mm});
            skLineSegment(sketch, "E318", {"start": v(106.55, 76.9) * mm, "end": v(106.54, 76.78) * mm});
            skLineSegment(sketch, "E319", {"start": v(106.54, 76.78) * mm, "end": v(106.54, 76.67) * mm});
            skLineSegment(sketch, "E320", {"start": v(106.54, 76.67) * mm, "end": v(106.53, 76.57) * mm});
            skLineSegment(sketch, "E321", {"start": v(106.53, 76.57) * mm, "end": v(106.51, 76.46) * mm});
            skLineSegment(sketch, "E322", {"start": v(106.51, 76.46) * mm, "end": v(106.5, 76.35) * mm});
            skLineSegment(sketch, "E323", {"start": v(106.5, 76.35) * mm, "end": v(106.48, 76.24) * mm});
            skLineSegment(sketch, "E324", {"start": v(106.48, 76.24) * mm, "end": v(106.47, 76.14) * mm});
            skLineSegment(sketch, "E325", {"start": v(106.47, 76.14) * mm, "end": v(106.45, 76.04) * mm});
            skLineSegment(sketch, "E326", {"start": v(106.45, 76.04) * mm, "end": v(106.42, 75.93) * mm});
            skLineSegment(sketch, "E327", {"start": v(106.42, 75.93) * mm, "end": v(106.4, 75.83) * mm});
            skLineSegment(sketch, "E328", {"start": v(106.4, 75.83) * mm, "end": v(106.37, 75.73) * mm});
            skLineSegment(sketch, "E329", {"start": v(106.37, 75.73) * mm, "end": v(106.34, 75.64) * mm});
            skLineSegment(sketch, "E330", {"start": v(106.34, 75.64) * mm, "end": v(106.31, 75.54) * mm});
            skLineSegment(sketch, "E331", {"start": v(106.31, 75.54) * mm, "end": v(106.28, 75.45) * mm});
            skLineSegment(sketch, "E332", {"start": v(106.28, 75.45) * mm, "end": v(106.25, 75.35) * mm});
            skLineSegment(sketch, "E333", {"start": v(106.25, 75.35) * mm, "end": v(106.21, 75.26) * mm});
            skLineSegment(sketch, "E334", {"start": v(106.21, 75.26) * mm, "end": v(106.17, 75.17) * mm});
            skLineSegment(sketch, "E335", {"start": v(106.17, 75.17) * mm, "end": v(106.13, 75.09) * mm});
            skLineSegment(sketch, "E336", {"start": v(106.13, 75.09) * mm, "end": v(106.09, 75) * mm});
            skLineSegment(sketch, "E337", {"start": v(106.09, 75) * mm, "end": v(106.05, 74.92) * mm});
            skLineSegment(sketch, "E338", {"start": v(106.05, 74.92) * mm, "end": v(106, 74.84) * mm});
            skLineSegment(sketch, "E339", {"start": v(106, 74.84) * mm, "end": v(105.95, 74.76) * mm});
            skLineSegment(sketch, "E340", {"start": v(105.95, 74.76) * mm, "end": v(105.9, 74.68) * mm});
            skLineSegment(sketch, "E341", {"start": v(105.9, 74.68) * mm, "end": v(105.85, 74.6) * mm});
            skLineSegment(sketch, "E342", {"start": v(105.85, 74.6) * mm, "end": v(105.8, 74.53) * mm});
            skLineSegment(sketch, "E343", {"start": v(105.8, 74.53) * mm, "end": v(105.74, 74.46) * mm});
            skLineSegment(sketch, "E344", {"start": v(105.74, 74.46) * mm, "end": v(105.69, 74.4) * mm});
            skLineSegment(sketch, "E345", {"start": v(105.69, 74.4) * mm, "end": v(105.63, 74.33) * mm});
            skLineSegment(sketch, "E346", {"start": v(105.63, 74.33) * mm, "end": v(105.57, 74.27) * mm});
            skLineSegment(sketch, "E347", {"start": v(105.57, 74.27) * mm, "end": v(105.51, 74.2) * mm});
            skLineSegment(sketch, "E348", {"start": v(105.51, 74.2) * mm, "end": v(105.45, 74.15) * mm});
            skLineSegment(sketch, "E349", {"start": v(105.45, 74.15) * mm, "end": v(105.39, 74.1) * mm});
            skLineSegment(sketch, "E350", {"start": v(105.39, 74.1) * mm, "end": v(105.32, 74.04) * mm});
            skLineSegment(sketch, "E351", {"start": v(105.32, 74.04) * mm, "end": v(105.26, 74) * mm});
            skLineSegment(sketch, "E352", {"start": v(105.26, 74) * mm, "end": v(105.19, 73.95) * mm});
            skLineSegment(sketch, "E353", {"start": v(105.19, 73.95) * mm, "end": v(105.12, 73.9) * mm});
            skLineSegment(sketch, "E354", {"start": v(105.12, 73.9) * mm, "end": v(105.05, 73.86) * mm});
            skLineSegment(sketch, "E355", {"start": v(105.05, 73.86) * mm, "end": v(104.98, 73.82) * mm});
            skLineSegment(sketch, "E356", {"start": v(104.98, 73.82) * mm, "end": v(104.9, 73.79) * mm});
            skLineSegment(sketch, "E357", {"start": v(104.9, 73.79) * mm, "end": v(104.83, 73.76) * mm});
            skLineSegment(sketch, "E358", {"start": v(104.83, 73.76) * mm, "end": v(104.76, 73.73) * mm});
            skLineSegment(sketch, "E359", {"start": v(104.76, 73.73) * mm, "end": v(104.69, 73.7) * mm});
            skLineSegment(sketch, "E360", {"start": v(104.69, 73.7) * mm, "end": v(104.6, 73.68) * mm});
            skLineSegment(sketch, "E361", {"start": v(104.6, 73.68) * mm, "end": v(104.53, 73.65) * mm});
            skLineSegment(sketch, "E362", {"start": v(104.53, 73.65) * mm, "end": v(104.46, 73.64) * mm});
            skLineSegment(sketch, "E363", {"start": v(104.46, 73.64) * mm, "end": v(104.38, 73.62) * mm});
            skLineSegment(sketch, "E364", {"start": v(104.38, 73.62) * mm, "end": v(104.3, 73.6) * mm});
            skLineSegment(sketch, "E365", {"start": v(104.3, 73.6) * mm, "end": v(104.22, 73.6) * mm});
            skLineSegment(sketch, "E366", {"start": v(104.22, 73.6) * mm, "end": v(104.14, 73.6) * mm});
            skLineSegment(sketch, "E367", {"start": v(104.14, 73.6) * mm, "end": v(104.06, 73.59) * mm});
            skLineSegment(sketch, "E368", {"start": v(104.06, 73.59) * mm, "end": v(103.98, 73.59) * mm});
            skLineSegment(sketch, "E369", {"start": v(103.98, 73.59) * mm, "end": v(103.9, 73.6) * mm});
            skLineSegment(sketch, "E370", {"start": v(103.9, 73.6) * mm, "end": v(103.82, 73.6) * mm});
            skLineSegment(sketch, "E371", {"start": v(103.82, 73.6) * mm, "end": v(103.73, 73.6) * mm});
            skLineSegment(sketch, "E372", {"start": v(103.73, 73.6) * mm, "end": v(103.65, 73.62) * mm});
            skLineSegment(sketch, "E373", {"start": v(103.65, 73.62) * mm, "end": v(103.57, 73.63) * mm});
            skLineSegment(sketch, "E374", {"start": v(103.57, 73.63) * mm, "end": v(103.49, 73.65) * mm});
            skLineSegment(sketch, "E375", {"start": v(103.49, 73.65) * mm, "end": v(103.4, 73.67) * mm});
            skLineSegment(sketch, "E376", {"start": v(103.4, 73.67) * mm, "end": v(103.32, 73.7) * mm});
            skLineSegment(sketch, "E377", {"start": v(103.32, 73.7) * mm, "end": v(103.24, 73.72) * mm});
            skLineSegment(sketch, "E378", {"start": v(103.24, 73.72) * mm, "end": v(103.16, 73.75) * mm});
            skLineSegment(sketch, "E379", {"start": v(103.16, 73.75) * mm, "end": v(103.08, 73.78) * mm});
            skLineSegment(sketch, "E380", {"start": v(103.08, 73.78) * mm, "end": v(103, 73.82) * mm});
            skLineSegment(sketch, "E381", {"start": v(103, 73.82) * mm, "end": v(102.91, 73.86) * mm});
            skLineSegment(sketch, "E382", {"start": v(102.91, 73.86) * mm, "end": v(102.83, 73.9) * mm});
            skLineSegment(sketch, "E383", {"start": v(102.83, 73.9) * mm, "end": v(102.75, 73.94) * mm});
            skLineSegment(sketch, "E384", {"start": v(102.75, 73.94) * mm, "end": v(102.67, 73.99) * mm});
            skLineSegment(sketch, "E385", {"start": v(102.67, 73.99) * mm, "end": v(102.59, 74.04) * mm});
            skLineSegment(sketch, "E386", {"start": v(102.59, 74.04) * mm, "end": v(102.51, 74.09) * mm});
            skLineSegment(sketch, "E387", {"start": v(102.51, 74.09) * mm, "end": v(102.43, 74.14) * mm});
            skLineSegment(sketch, "E388", {"start": v(102.43, 74.14) * mm, "end": v(102.35, 74.2) * mm});
            skLineSegment(sketch, "E389", {"start": v(102.35, 74.2) * mm, "end": v(102.28, 74.26) * mm});
            skLineSegment(sketch, "E390", {"start": v(102.28, 74.26) * mm, "end": v(102.2, 74.32) * mm});
            skLineSegment(sketch, "E391", {"start": v(102.2, 74.32) * mm, "end": v(102.12, 74.39) * mm});
            skLineSegment(sketch, "E392", {"start": v(102.12, 74.39) * mm, "end": v(102.05, 74.45) * mm});
            skLineSegment(sketch, "E393", {"start": v(102.05, 74.45) * mm, "end": v(101.98, 74.52) * mm});
            skLineSegment(sketch, "E394", {"start": v(101.98, 74.52) * mm, "end": v(101.9, 74.6) * mm});
            skLineSegment(sketch, "E395", {"start": v(101.9, 74.6) * mm, "end": v(101.83, 74.67) * mm});
            skLineSegment(sketch, "E396", {"start": v(101.83, 74.67) * mm, "end": v(101.76, 74.74) * mm});
            skLineSegment(sketch, "E397", {"start": v(101.76, 74.74) * mm, "end": v(101.69, 74.82) * mm});
            skLineSegment(sketch, "E398", {"start": v(101.69, 74.82) * mm, "end": v(101.62, 74.9) * mm});
            skLineSegment(sketch, "E399", {"start": v(101.62, 74.9) * mm, "end": v(101.55, 74.99) * mm});
            skLineSegment(sketch, "E400", {"start": v(101.55, 74.99) * mm, "end": v(101.49, 75.07) * mm});
            skLineSegment(sketch, "E401", {"start": v(101.49, 75.07) * mm, "end": v(101.42, 75.16) * mm});
            skLineSegment(sketch, "E402", {"start": v(101.42, 75.16) * mm, "end": v(101.36, 75.25) * mm});
            skLineSegment(sketch, "E403", {"start": v(101.36, 75.25) * mm, "end": v(101.3, 75.34) * mm});
            skLineSegment(sketch, "E404", {"start": v(101.3, 75.34) * mm, "end": v(101.24, 75.43) * mm});
            skLineSegment(sketch, "E405", {"start": v(101.24, 75.43) * mm, "end": v(101.18, 75.52) * mm});
            skLineSegment(sketch, "E406", {"start": v(101.18, 75.52) * mm, "end": v(101.12, 75.62) * mm});
            skLineSegment(sketch, "E407", {"start": v(101.12, 75.62) * mm, "end": v(101.06, 75.72) * mm});
            skLineSegment(sketch, "E408", {"start": v(101.06, 75.72) * mm, "end": v(101.01, 75.82) * mm});
            skLineSegment(sketch, "E409", {"start": v(101.01, 75.82) * mm, "end": v(100.96, 75.92) * mm});
            skLineSegment(sketch, "E410", {"start": v(100.96, 75.92) * mm, "end": v(100.9, 76.02) * mm});
            skLineSegment(sketch, "E411", {"start": v(100.9, 76.02) * mm, "end": v(100.86, 76.12) * mm});
            skLineSegment(sketch, "E412", {"start": v(100.86, 76.12) * mm, "end": v(100.8, 76.23) * mm});
            skLineSegment(sketch, "E413", {"start": v(100.8, 76.23) * mm, "end": v(100.76, 76.33) * mm});
            skLineSegment(sketch, "E414", {"start": v(100.76, 76.33) * mm, "end": v(100.72, 76.44) * mm});
            skLineSegment(sketch, "E415", {"start": v(100.72, 76.44) * mm, "end": v(100.68, 76.55) * mm});
            skLineSegment(sketch, "E416", {"start": v(100.68, 76.55) * mm, "end": v(100.64, 76.66) * mm});
            skLineSegment(sketch, "E417", {"start": v(100.64, 76.66) * mm, "end": v(100.6, 76.77) * mm});
            skLineSegment(sketch, "E418", {"start": v(100.6, 76.77) * mm, "end": v(100.56, 76.88) * mm});
            skLineSegment(sketch, "E419", {"start": v(100.56, 76.88) * mm, "end": v(100.53, 76.99) * mm});
            skLineSegment(sketch, "E420", {"start": v(100.53, 76.99) * mm, "end": v(100.5, 77.1) * mm});
            skLineSegment(sketch, "E421", {"start": v(100.5, 77.1) * mm, "end": v(100.47, 77.21) * mm});
            skLineSegment(sketch, "E422", {"start": v(100.47, 77.21) * mm, "end": v(100.44, 77.32) * mm});
            skLineSegment(sketch, "E423", {"start": v(100.44, 77.32) * mm, "end": v(100.41, 77.44) * mm});
            skLineSegment(sketch, "E424", {"start": v(100.41, 77.44) * mm, "end": v(100.39, 77.55) * mm});
            skLineSegment(sketch, "E425", {"start": v(100.39, 77.55) * mm, "end": v(100.36, 77.67) * mm});
            skLineSegment(sketch, "E426", {"start": v(100.36, 77.67) * mm, "end": v(100.34, 77.78) * mm});
            skLineSegment(sketch, "E427", {"start": v(100.34, 77.78) * mm, "end": v(100.32, 77.9) * mm});
            skLineSegment(sketch, "E428", {"start": v(100.32, 77.9) * mm, "end": v(100.3, 78) * mm});
            skLineSegment(sketch, "E429", {"start": v(100.3, 78) * mm, "end": v(100.3, 78.12) * mm});
            skLineSegment(sketch, "E430", {"start": v(100.3, 78.12) * mm, "end": v(100.28, 78.24) * mm});
            skLineSegment(sketch, "E431", {"start": v(100.28, 78.24) * mm, "end": v(100.27, 78.35) * mm});
            skLineSegment(sketch, "E432", {"start": v(100.27, 78.35) * mm, "end": v(100.27, 78.47) * mm});
            skLineSegment(sketch, "E433", {"start": v(100.27, 78.47) * mm, "end": v(100.26, 78.58) * mm});
            skLineSegment(sketch, "E434", {"start": v(100.26, 78.58) * mm, "end": v(100.26, 78.7) * mm});
            skLineSegment(sketch, "E435", {"start": v(100.26, 78.7) * mm, "end": v(100.26, 78.8) * mm});
            skLineSegment(sketch, "E436", {"start": v(100.26, 78.8) * mm, "end": v(100.26, 78.92) * mm});
            skLineSegment(sketch, "E437", {"start": v(100.26, 78.92) * mm, "end": v(100.26, 79.03) * mm});
            skLineSegment(sketch, "E438", {"start": v(100.26, 79.03) * mm, "end": v(100.27, 79.14) * mm});
            skLineSegment(sketch, "E439", {"start": v(100.27, 79.14) * mm, "end": v(100.27, 79.25) * mm});
            skLineSegment(sketch, "E440", {"start": v(100.27, 79.25) * mm, "end": v(100.28, 79.36) * mm});
            skLineSegment(sketch, "E441", {"start": v(100.28, 79.36) * mm, "end": v(100.3, 79.47) * mm});
            skLineSegment(sketch, "E442", {"start": v(100.3, 79.47) * mm, "end": v(100.3, 79.57) * mm});
            skLineSegment(sketch, "E443", {"start": v(100.3, 79.57) * mm, "end": v(100.32, 79.68) * mm});
            skLineSegment(sketch, "E444", {"start": v(100.32, 79.68) * mm, "end": v(100.34, 79.78) * mm});
            skLineSegment(sketch, "E445", {"start": v(100.34, 79.78) * mm, "end": v(100.36, 79.89) * mm});
            skLineSegment(sketch, "E446", {"start": v(100.36, 79.89) * mm, "end": v(100.39, 79.99) * mm});
            skLineSegment(sketch, "E447", {"start": v(100.39, 79.99) * mm, "end": v(100.41, 80.09) * mm});
            skLineSegment(sketch, "E448", {"start": v(100.41, 80.09) * mm, "end": v(100.44, 80.19) * mm});
            skLineSegment(sketch, "E449", {"start": v(100.44, 80.19) * mm, "end": v(100.47, 80.29) * mm});
            skLineSegment(sketch, "E450", {"start": v(100.47, 80.29) * mm, "end": v(100.5, 80.38) * mm});
            skLineSegment(sketch, "E451", {"start": v(100.5, 80.38) * mm, "end": v(100.53, 80.48) * mm});
            skLineSegment(sketch, "E452", {"start": v(100.53, 80.48) * mm, "end": v(100.56, 80.57) * mm});
            skLineSegment(sketch, "E453", {"start": v(100.56, 80.57) * mm, "end": v(100.6, 80.66) * mm});
            skLineSegment(sketch, "E454", {"start": v(100.6, 80.66) * mm, "end": v(100.64, 80.75) * mm});
            skLineSegment(sketch, "E455", {"start": v(100.64, 80.75) * mm, "end": v(100.68, 80.84) * mm});
            skLineSegment(sketch, "E456", {"start": v(100.68, 80.84) * mm, "end": v(100.72, 80.92) * mm});
            skLineSegment(sketch, "E457", {"start": v(100.72, 80.92) * mm, "end": v(100.76, 81) * mm});
            skLineSegment(sketch, "E458", {"start": v(100.76, 81) * mm, "end": v(100.8, 81.09) * mm});
            skLineSegment(sketch, "E459", {"start": v(100.8, 81.09) * mm, "end": v(100.86, 81.17) * mm});
            skLineSegment(sketch, "E460", {"start": v(100.86, 81.17) * mm, "end": v(100.9, 81.24) * mm});
            skLineSegment(sketch, "E461", {"start": v(100.9, 81.24) * mm, "end": v(100.96, 81.32) * mm});
            skLineSegment(sketch, "E462", {"start": v(100.96, 81.32) * mm, "end": v(101.01, 81.39) * mm});
            skLineSegment(sketch, "E463", {"start": v(101.01, 81.39) * mm, "end": v(101.06, 81.46) * mm});
            skLineSegment(sketch, "E464", {"start": v(101.06, 81.46) * mm, "end": v(101.12, 81.53) * mm});
            skLineSegment(sketch, "E465", {"start": v(101.12, 81.53) * mm, "end": v(101.18, 81.6) * mm});
            skLineSegment(sketch, "E466", {"start": v(101.18, 81.6) * mm, "end": v(101.24, 81.65) * mm});
            skLineSegment(sketch, "E467", {"start": v(101.24, 81.65) * mm, "end": v(101.3, 81.71) * mm});
            skLineSegment(sketch, "E468", {"start": v(101.3, 81.71) * mm, "end": v(101.36, 81.77) * mm});
            skLineSegment(sketch, "E469", {"start": v(101.36, 81.77) * mm, "end": v(101.42, 81.83) * mm});
            skLineSegment(sketch, "E470", {"start": v(101.42, 81.83) * mm, "end": v(101.49, 81.88) * mm});
            skLineSegment(sketch, "E471", {"start": v(101.49, 81.88) * mm, "end": v(101.55, 81.93) * mm});
            skLineSegment(sketch, "E472", {"start": v(101.55, 81.93) * mm, "end": v(101.62, 81.98) * mm});
            skLineSegment(sketch, "E473", {"start": v(101.62, 81.98) * mm, "end": v(101.69, 82.02) * mm});
            skLineSegment(sketch, "E474", {"start": v(101.69, 82.02) * mm, "end": v(101.76, 82.06) * mm});
            skLineSegment(sketch, "E475", {"start": v(101.76, 82.06) * mm, "end": v(101.83, 82.1) * mm});
            skLineSegment(sketch, "E476", {"start": v(101.83, 82.1) * mm, "end": v(101.9, 82.13) * mm});
            skLineSegment(sketch, "E477", {"start": v(101.9, 82.13) * mm, "end": v(101.98, 82.17) * mm});
            skLineSegment(sketch, "E478", {"start": v(101.98, 82.17) * mm, "end": v(102.05, 82.2) * mm});
            skLineSegment(sketch, "E479", {"start": v(102.05, 82.2) * mm, "end": v(102.12, 82.22) * mm});
            skLineSegment(sketch, "E480", {"start": v(102.12, 82.22) * mm, "end": v(102.2, 82.25) * mm});
            skLineSegment(sketch, "E481", {"start": v(102.2, 82.25) * mm, "end": v(102.28, 82.27) * mm});
            skLineSegment(sketch, "E482", {"start": v(102.28, 82.27) * mm, "end": v(102.35, 82.29) * mm});
            skLineSegment(sketch, "E483", {"start": v(102.35, 82.29) * mm, "end": v(102.43, 82.3) * mm});
            skLineSegment(sketch, "E484", {"start": v(102.43, 82.3) * mm, "end": v(102.51, 82.31) * mm});
            skLineSegment(sketch, "E485", {"start": v(102.51, 82.31) * mm, "end": v(102.59, 82.32) * mm});
            skLineSegment(sketch, "E486", {"start": v(102.59, 82.32) * mm, "end": v(102.67, 82.33) * mm});
            skLineSegment(sketch, "E487", {"start": v(102.67, 82.33) * mm, "end": v(102.75, 82.33) * mm});
            skLineSegment(sketch, "E488", {"start": v(102.75, 82.33) * mm, "end": v(102.83, 82.33) * mm});
            skLineSegment(sketch, "E489", {"start": v(102.83, 82.33) * mm, "end": v(102.91, 82.33) * mm});
            skLineSegment(sketch, "E490", {"start": v(102.91, 82.33) * mm, "end": v(103, 82.33) * mm});
            skLineSegment(sketch, "E491", {"start": v(103, 82.33) * mm, "end": v(103.08, 82.32) * mm});
            skLineSegment(sketch, "E492", {"start": v(103.08, 82.32) * mm, "end": v(103.16, 82.3) * mm});
            skLineSegment(sketch, "E493", {"start": v(103.16, 82.3) * mm, "end": v(103.24, 82.3) * mm});
            skLineSegment(sketch, "E494", {"start": v(103.24, 82.3) * mm, "end": v(103.32, 82.27) * mm});
            skLineSegment(sketch, "E495", {"start": v(103.32, 82.27) * mm, "end": v(103.4, 82.25) * mm});
            skLineSegment(sketch, "E496", {"start": v(103.4, 82.25) * mm, "end": v(103.49, 82.23) * mm});
            skLineSegment(sketch, "E497", {"start": v(103.49, 82.23) * mm, "end": v(103.57, 82.2) * mm});
            skLineSegment(sketch, "E498", {"start": v(103.57, 82.2) * mm, "end": v(103.65, 82.17) * mm});
            skLineSegment(sketch, "E499", {"start": v(103.65, 82.17) * mm, "end": v(103.73, 82.14) * mm});
            skLineSegment(sketch, "E500", {"start": v(103.73, 82.14) * mm, "end": v(103.82, 82.1) * mm});
            skLineSegment(sketch, "E501", {"start": v(103.82, 82.1) * mm, "end": v(103.9, 82.07) * mm});
            skLineSegment(sketch, "E502", {"start": v(103.9, 82.07) * mm, "end": v(103.98, 82.03) * mm});
            skLineSegment(sketch, "E503", {"start": v(103.98, 82.03) * mm, "end": v(104.06, 81.98) * mm});
            skLineSegment(sketch, "E504", {"start": v(104.06, 81.98) * mm, "end": v(104.14, 81.94) * mm});
            skLineSegment(sketch, "E505", {"start": v(104.14, 81.94) * mm, "end": v(104.22, 81.89) * mm});
            skLineSegment(sketch, "E506", {"start": v(104.22, 81.89) * mm, "end": v(104.3, 81.84) * mm});
            skLineSegment(sketch, "E507", {"start": v(104.3, 81.84) * mm, "end": v(104.38, 81.78) * mm});
            skLineSegment(sketch, "E508", {"start": v(104.38, 81.78) * mm, "end": v(104.46, 81.72) * mm});
            skLineSegment(sketch, "E509", {"start": v(104.46, 81.72) * mm, "end": v(104.53, 81.66) * mm});
            skLineSegment(sketch, "E510", {"start": v(104.53, 81.66) * mm, "end": v(104.6, 81.6) * mm});
            skLineSegment(sketch, "E511", {"start": v(104.6, 81.6) * mm, "end": v(104.69, 81.54) * mm});
            skLineSegment(sketch, "E512", {"start": v(104.69, 81.54) * mm, "end": v(104.76, 81.47) * mm});
            skLineSegment(sketch, "E513", {"start": v(104.76, 81.47) * mm, "end": v(104.83, 81.4) * mm});
            skLineSegment(sketch, "E514", {"start": v(104.83, 81.4) * mm, "end": v(104.9, 81.33) * mm});
            skLineSegment(sketch, "E515", {"start": v(104.9, 81.33) * mm, "end": v(104.98, 81.26) * mm});
            skLineSegment(sketch, "E516", {"start": v(104.98, 81.26) * mm, "end": v(105.05, 81.18) * mm});
            skLineSegment(sketch, "E517", {"start": v(105.05, 81.18) * mm, "end": v(105.12, 81.1) * mm});
            skLineSegment(sketch, "E518", {"start": v(105.12, 81.1) * mm, "end": v(105.19, 81.02) * mm});
            skLineSegment(sketch, "E519", {"start": v(105.19, 81.02) * mm, "end": v(105.26, 80.94) * mm});
            skLineSegment(sketch, "E520", {"start": v(105.26, 80.94) * mm, "end": v(105.32, 80.85) * mm});
            skLineSegment(sketch, "E521", {"start": v(105.32, 80.85) * mm, "end": v(105.39, 80.76) * mm});
            skLineSegment(sketch, "E522", {"start": v(105.39, 80.76) * mm, "end": v(105.45, 80.68) * mm});
            skLineSegment(sketch, "E523", {"start": v(105.45, 80.68) * mm, "end": v(105.51, 80.59) * mm});
            skLineSegment(sketch, "E524", {"start": v(105.51, 80.59) * mm, "end": v(105.57, 80.5) * mm});
            skLineSegment(sketch, "E525", {"start": v(105.57, 80.5) * mm, "end": v(105.63, 80.4) * mm});
            skLineSegment(sketch, "E526", {"start": v(105.63, 80.4) * mm, "end": v(105.69, 80.3) * mm});
            skLineSegment(sketch, "E527", {"start": v(105.69, 80.3) * mm, "end": v(105.74, 80.2) * mm});
            skLineSegment(sketch, "E528", {"start": v(105.74, 80.2) * mm, "end": v(105.8, 80.1) * mm});
            skLineSegment(sketch, "E529", {"start": v(105.8, 80.1) * mm, "end": v(105.85, 80) * mm});
            skLineSegment(sketch, "E530", {"start": v(105.85, 80) * mm, "end": v(105.9, 79.9) * mm});
            skLineSegment(sketch, "E531", {"start": v(105.9, 79.9) * mm, "end": v(105.95, 79.8) * mm});
            skLineSegment(sketch, "E532", {"start": v(105.95, 79.8) * mm, "end": v(106, 79.7) * mm});
            skLineSegment(sketch, "E533", {"start": v(106, 79.7) * mm, "end": v(106.05, 79.6) * mm});
            skLineSegment(sketch, "E534", {"start": v(106.05, 79.6) * mm, "end": v(106.09, 79.48) * mm});
            skLineSegment(sketch, "E535", {"start": v(106.09, 79.48) * mm, "end": v(106.13, 79.38) * mm});
            skLineSegment(sketch, "E536", {"start": v(106.13, 79.38) * mm, "end": v(106.17, 79.27) * mm});
            skLineSegment(sketch, "E537", {"start": v(106.17, 79.27) * mm, "end": v(106.21, 79.16) * mm});
            skLineSegment(sketch, "E538", {"start": v(106.21, 79.16) * mm, "end": v(106.25, 79.05) * mm});
            skLineSegment(sketch, "E539", {"start": v(106.25, 79.05) * mm, "end": v(106.28, 78.94) * mm});
            skLineSegment(sketch, "E540", {"start": v(106.28, 78.94) * mm, "end": v(106.31, 78.82) * mm});
            skLineSegment(sketch, "E541", {"start": v(106.31, 78.82) * mm, "end": v(106.34, 78.71) * mm});
            skLineSegment(sketch, "E542", {"start": v(106.34, 78.71) * mm, "end": v(106.37, 78.6) * mm});
            skLineSegment(sketch, "E543", {"start": v(106.37, 78.6) * mm, "end": v(106.4, 78.49) * mm});
            skLineSegment(sketch, "E544", {"start": v(106.4, 78.49) * mm, "end": v(106.42, 78.37) * mm});
            skLineSegment(sketch, "E545", {"start": v(106.42, 78.37) * mm, "end": v(106.45, 78.26) * mm});
            skLineSegment(sketch, "E546", {"start": v(106.45, 78.26) * mm, "end": v(106.47, 78.14) * mm});
            skLineSegment(sketch, "E547", {"start": v(106.47, 78.14) * mm, "end": v(106.48, 78.03) * mm});
            skLineSegment(sketch, "E548", {"start": v(106.48, 78.03) * mm, "end": v(106.5, 77.91) * mm});
            skLineSegment(sketch, "E549", {"start": v(106.5, 77.91) * mm, "end": v(106.51, 77.8) * mm});
            skLineSegment(sketch, "E550", {"start": v(106.51, 77.8) * mm, "end": v(106.53, 77.69) * mm});
            skLineSegment(sketch, "E551", {"start": v(106.53, 77.69) * mm, "end": v(106.54, 77.57) * mm});
            skLineSegment(sketch, "E552", {"start": v(106.54, 77.57) * mm, "end": v(106.54, 77.46) * mm});
            skLineSegment(sketch, "E553", {"start": v(106.54, 77.46) * mm, "end": v(106.55, 77.34) * mm});
            skLineSegment(sketch, "E554", {"start": v(106.55, 77.34) * mm, "end": v(106.55, 77.23) * mm});
            skLineSegment(sketch, "E555", {"start": v(106.55, 77.23) * mm, "end": v(106.55, 77.12) * mm});
            skLineSegment(sketch, "E556", {"start": v(117.97, 83.39) * mm, "end": v(114.6, 82.49) * mm});
            skLineSegment(sketch, "E557", {"start": v(119.53, 81.35) * mm, "end": v(116.16, 80.44) * mm});
            skLineSegment(sketch, "E558", {"start": v(119.53, 81.35) * mm, "end": v(117.97, 83.39) * mm});
            skLineSegment(sketch, "E559", {"start": v(117.16, 85.54) * mm, "end": v(113.79, 84.63) * mm});
            skLineSegment(sketch, "E560", {"start": v(118.85, 83.74) * mm, "end": v(115.49, 82.84) * mm});
            skLineSegment(sketch, "E561", {"start": v(118.85, 83.74) * mm, "end": v(117.16, 85.54) * mm});
            skLineSegment(sketch, "E562", {"start": v(119.98, 78.9) * mm, "end": v(116.62, 78) * mm});
            skLineSegment(sketch, "E563", {"start": v(119.98, 78.9) * mm, "end": v(118.63, 81.1) * mm});
            skLineSegment(sketch, "E564", {"start": v(116.16, 87.57) * mm, "end": v(112.8, 86.67) * mm});
            skLineSegment(sketch, "E565", {"start": v(117.97, 86.06) * mm, "end": v(114.6, 85.16) * mm});
            skLineSegment(sketch, "E566", {"start": v(117.97, 86.06) * mm, "end": v(116.16, 87.57) * mm});
            skLineSegment(sketch, "E567", {"start": v(117.97, 83.39) * mm, "end": v(118.85, 83.74) * mm});
            skLineSegment(sketch, "E568", {"start": v(120.21, 76.46) * mm, "end": v(116.85, 75.56) * mm});
            skLineSegment(sketch, "E569", {"start": v(120.21, 76.46) * mm, "end": v(119.13, 78.68) * mm});
            skLineSegment(sketch, "E570", {"start": v(117.16, 85.54) * mm, "end": v(117.97, 86.06) * mm});
            skLineSegment(sketch, "E571", {"start": v(115, 89.45) * mm, "end": v(111.64, 88.55) * mm});
            skLineSegment(sketch, "E572", {"start": v(116.9, 88.25) * mm, "end": v(113.53, 87.35) * mm});
            skLineSegment(sketch, "E573", {"start": v(116.9, 88.25) * mm, "end": v(115, 89.45) * mm});
            skLineSegment(sketch, "E574", {"start": v(120.21, 74.06) * mm, "end": v(116.85, 73.16) * mm});
            skLineSegment(sketch, "E575", {"start": v(120.21, 74.06) * mm, "end": v(119.39, 76.24) * mm});
            skLineSegment(sketch, "E576", {"start": v(116.16, 87.57) * mm, "end": v(116.9, 88.25) * mm});
            skLineSegment(sketch, "E577", {"start": v(113.71, 91.15) * mm, "end": v(110.34, 90.25) * mm});
            skLineSegment(sketch, "E578", {"start": v(115.65, 90.28) * mm, "end": v(112.29, 89.38) * mm});
            skLineSegment(sketch, "E579", {"start": v(115.65, 90.28) * mm, "end": v(113.71, 91.15) * mm});
            skLineSegment(sketch, "E580", {"start": v(119.98, 71.74) * mm, "end": v(116.62, 70.84) * mm});
            skLineSegment(sketch, "E581", {"start": v(119.98, 71.74) * mm, "end": v(119.4, 73.84) * mm});
            skLineSegment(sketch, "E582", {"start": v(115, 89.45) * mm, "end": v(115.65, 90.28) * mm});
            skLineSegment(sketch, "E583", {"start": v(112.3, 92.65) * mm, "end": v(108.93, 91.74) * mm});
            skLineSegment(sketch, "E584", {"start": v(114.26, 92.12) * mm, "end": v(110.89, 91.22) * mm});
            skLineSegment(sketch, "E585", {"start": v(114.26, 92.12) * mm, "end": v(112.3, 92.65) * mm});
            skLineSegment(sketch, "E586", {"start": v(113.71, 91.15) * mm, "end": v(114.26, 92.12) * mm});
            skLineSegment(sketch, "E587", {"start": v(119.53, 69.55) * mm, "end": v(116.16, 68.64) * mm});
            skLineSegment(sketch, "E588", {"start": v(119.53, 69.55) * mm, "end": v(119.16, 71.52) * mm});
            skLineSegment(sketch, "E589", {"start": v(110.79, 93.9) * mm, "end": v(107.42, 93) * mm});
            skLineSegment(sketch, "E590", {"start": v(112.73, 93.73) * mm, "end": v(109.36, 92.83) * mm});
            skLineSegment(sketch, "E591", {"start": v(112.73, 93.73) * mm, "end": v(110.79, 93.9) * mm});
            skLineSegment(sketch, "E592", {"start": v(112.3, 92.65) * mm, "end": v(112.73, 93.73) * mm});
            skLineSegment(sketch, "E593", {"start": v(118.85, 67.5) * mm, "end": v(115.49, 66.6) * mm});
            skLineSegment(sketch, "E594", {"start": v(118.85, 67.5) * mm, "end": v(118.68, 69.32) * mm});
            skLineSegment(sketch, "E595", {"start": v(109.2, 94.9) * mm, "end": v(105.84, 94) * mm});
            skLineSegment(sketch, "E596", {"start": v(111.1, 95.08) * mm, "end": v(107.73, 94.18) * mm});
            skLineSegment(sketch, "E597", {"start": v(111.1, 95.08) * mm, "end": v(109.2, 94.9) * mm});
            skLineSegment(sketch, "E598", {"start": v(110.79, 93.9) * mm, "end": v(111.1, 95.08) * mm});
            skLineSegment(sketch, "E599", {"start": v(117.97, 65.67) * mm, "end": v(114.6, 64.76) * mm});
            skLineSegment(sketch, "E600", {"start": v(117.97, 65.67) * mm, "end": v(117.97, 67.27) * mm});
            skLineSegment(sketch, "E601", {"start": v(109.4, 96.16) * mm, "end": v(106.03, 95.26) * mm});
            skLineSegment(sketch, "E602", {"start": v(109.2, 94.9) * mm, "end": v(109.4, 96.16) * mm});
            skLineSegment(sketch, "E603", {"start": v(116.9, 64.05) * mm, "end": v(113.53, 63.15) * mm});
            skLineSegment(sketch, "E604", {"start": v(116.9, 64.05) * mm, "end": v(117.04, 65.42) * mm});
            skLineSegment(sketch, "E605", {"start": v(107.65, 96.94) * mm, "end": v(104.29, 96.04) * mm});
            skLineSegment(sketch, "E606", {"start": v(107.6, 95.68) * mm, "end": v(107.65, 96.94) * mm});
            skLineSegment(sketch, "E607", {"start": v(115.65, 62.69) * mm, "end": v(112.29, 61.78) * mm});
            skLineSegment(sketch, "E608", {"start": v(115.65, 62.69) * mm, "end": v(115.88, 63.78) * mm});
            skLineSegment(sketch, "E609", {"start": v(114.26, 61.6) * mm, "end": v(110.89, 60.7) * mm});
            skLineSegment(sketch, "E610", {"start": v(114.26, 61.6) * mm, "end": v(114.52, 62.38) * mm});
            skLineSegment(sketch, "E611", {"start": v(105.9, 97.41) * mm, "end": v(102.52, 96.51) * mm});
            skLineSegment(sketch, "E612", {"start": v(105.94, 96.48) * mm, "end": v(105.9, 97.41) * mm});
            skLineSegment(sketch, "E613", {"start": v(105.72, 80.25) * mm, "end": v(105.7, 80.27) * mm});
            skLineSegment(sketch, "E614", {"start": v(105.7, 80.27) * mm, "end": v(105.65, 80.37) * mm});
            skLineSegment(sketch, "E615", {"start": v(105.65, 80.37) * mm, "end": v(105.6, 80.46) * mm});
            skLineSegment(sketch, "E616", {"start": v(105.6, 80.46) * mm, "end": v(105.53, 80.55) * mm});
            skLineSegment(sketch, "E617", {"start": v(105.53, 80.55) * mm, "end": v(105.47, 80.64) * mm});
            skLineSegment(sketch, "E618", {"start": v(105.47, 80.64) * mm, "end": v(105.4, 80.73) * mm});
            skLineSegment(sketch, "E619", {"start": v(105.4, 80.73) * mm, "end": v(105.35, 80.81) * mm});
            skLineSegment(sketch, "E620", {"start": v(105.35, 80.81) * mm, "end": v(105.28, 80.9) * mm});
            skLineSegment(sketch, "E621", {"start": v(105.28, 80.9) * mm, "end": v(105.21, 80.98) * mm});
            skLineSegment(sketch, "E622", {"start": v(105.21, 80.98) * mm, "end": v(105.15, 81.06) * mm});
            skLineSegment(sketch, "E623", {"start": v(105.15, 81.06) * mm, "end": v(105.08, 81.13) * mm});
            skLineSegment(sketch, "E624", {"start": v(105.08, 81.13) * mm, "end": v(105, 81.2) * mm});
            skLineSegment(sketch, "E625", {"start": v(105, 81.2) * mm, "end": v(104.94, 81.28) * mm});
            skLineSegment(sketch, "E626", {"start": v(104.94, 81.28) * mm, "end": v(104.87, 81.35) * mm});
            skLineSegment(sketch, "E627", {"start": v(104.87, 81.35) * mm, "end": v(104.8, 81.42) * mm});
            skLineSegment(sketch, "E628", {"start": v(104.8, 81.42) * mm, "end": v(104.72, 81.48) * mm});
            skLineSegment(sketch, "E629", {"start": v(104.72, 81.48) * mm, "end": v(104.65, 81.55) * mm});
            skLineSegment(sketch, "E630", {"start": v(104.65, 81.55) * mm, "end": v(104.57, 81.6) * mm});
            skLineSegment(sketch, "E631", {"start": v(104.57, 81.6) * mm, "end": v(104.5, 81.67) * mm});
            skLineSegment(sketch, "E632", {"start": v(104.5, 81.67) * mm, "end": v(104.42, 81.72) * mm});
            skLineSegment(sketch, "E633", {"start": v(104.42, 81.72) * mm, "end": v(104.34, 81.78) * mm});
            skLineSegment(sketch, "E634", {"start": v(104.34, 81.78) * mm, "end": v(104.27, 81.83) * mm});
            skLineSegment(sketch, "E635", {"start": v(104.27, 81.83) * mm, "end": v(104.19, 81.87) * mm});
            skLineSegment(sketch, "E636", {"start": v(104.19, 81.87) * mm, "end": v(104.1, 81.92) * mm});
            skLineSegment(sketch, "E637", {"start": v(104.1, 81.92) * mm, "end": v(104.03, 81.96) * mm});
            skLineSegment(sketch, "E638", {"start": v(104.03, 81.96) * mm, "end": v(103.95, 82) * mm});
            skLineSegment(sketch, "E639", {"start": v(103.95, 82) * mm, "end": v(103.87, 82.04) * mm});
            skLineSegment(sketch, "E640", {"start": v(103.87, 82.04) * mm, "end": v(103.79, 82.07) * mm});
            skLineSegment(sketch, "E641", {"start": v(103.79, 82.07) * mm, "end": v(103.7, 82.1) * mm});
            skLineSegment(sketch, "E642", {"start": v(103.7, 82.1) * mm, "end": v(103.63, 82.14) * mm});
            skLineSegment(sketch, "E643", {"start": v(103.63, 82.14) * mm, "end": v(103.55, 82.16) * mm});
            skLineSegment(sketch, "E644", {"start": v(103.55, 82.16) * mm, "end": v(103.47, 82.18) * mm});
            skLineSegment(sketch, "E645", {"start": v(103.47, 82.18) * mm, "end": v(103.39, 82.2) * mm});
            skLineSegment(sketch, "E646", {"start": v(103.39, 82.2) * mm, "end": v(103.3, 82.22) * mm});
            skLineSegment(sketch, "E647", {"start": v(103.3, 82.22) * mm, "end": v(103.22, 82.24) * mm});
            skLineSegment(sketch, "E648", {"start": v(103.22, 82.24) * mm, "end": v(103.14, 82.25) * mm});
            skLineSegment(sketch, "E649", {"start": v(103.14, 82.25) * mm, "end": v(103.06, 82.26) * mm});
            skLineSegment(sketch, "E650", {"start": v(103.06, 82.26) * mm, "end": v(102.98, 82.26) * mm});
            skLineSegment(sketch, "E651", {"start": v(102.98, 82.26) * mm, "end": v(102.9, 82.26) * mm});
            skLineSegment(sketch, "E652", {"start": v(102.9, 82.26) * mm, "end": v(102.82, 82.26) * mm});
            skLineSegment(sketch, "E653", {"start": v(102.82, 82.26) * mm, "end": v(102.75, 82.26) * mm});
            skLineSegment(sketch, "E654", {"start": v(102.75, 82.26) * mm, "end": v(102.67, 82.25) * mm});
            skLineSegment(sketch, "E655", {"start": v(102.67, 82.25) * mm, "end": v(102.59, 82.25) * mm});
            skLineSegment(sketch, "E656", {"start": v(102.59, 82.25) * mm, "end": v(102.51, 82.23) * mm});
            skLineSegment(sketch, "E657", {"start": v(102.51, 82.23) * mm, "end": v(102.44, 82.22) * mm});
            skLineSegment(sketch, "E658", {"start": v(102.44, 82.22) * mm, "end": v(102.36, 82.2) * mm});
            skLineSegment(sketch, "E659", {"start": v(102.36, 82.2) * mm, "end": v(102.29, 82.18) * mm});
            skLineSegment(sketch, "E660", {"start": v(102.29, 82.18) * mm, "end": v(102.21, 82.16) * mm});
            skLineSegment(sketch, "E661", {"start": v(102.21, 82.16) * mm, "end": v(102.14, 82.13) * mm});
            skLineSegment(sketch, "E662", {"start": v(102.14, 82.13) * mm, "end": v(102.06, 82.1) * mm});
            skLineSegment(sketch, "E663", {"start": v(102.06, 82.1) * mm, "end": v(102, 82.07) * mm});
            skLineSegment(sketch, "E664", {"start": v(102, 82.07) * mm, "end": v(101.92, 82.03) * mm});
            skLineSegment(sketch, "E665", {"start": v(101.92, 82.03) * mm, "end": v(101.85, 82) * mm});
            skLineSegment(sketch, "E666", {"start": v(101.85, 82) * mm, "end": v(101.79, 81.96) * mm});
            skLineSegment(sketch, "E667", {"start": v(101.79, 81.96) * mm, "end": v(101.72, 81.91) * mm});
            skLineSegment(sketch, "E668", {"start": v(101.72, 81.91) * mm, "end": v(101.65, 81.87) * mm});
            skLineSegment(sketch, "E669", {"start": v(101.65, 81.87) * mm, "end": v(101.59, 81.82) * mm});
            skLineSegment(sketch, "E670", {"start": v(101.59, 81.82) * mm, "end": v(101.52, 81.77) * mm});
            skLineSegment(sketch, "E671", {"start": v(101.52, 81.77) * mm, "end": v(101.46, 81.71) * mm});
            skLineSegment(sketch, "E672", {"start": v(101.46, 81.71) * mm, "end": v(101.4, 81.66) * mm});
            skLineSegment(sketch, "E673", {"start": v(101.4, 81.66) * mm, "end": v(101.34, 81.6) * mm});
            skLineSegment(sketch, "E674", {"start": v(101.34, 81.6) * mm, "end": v(101.28, 81.54) * mm});
            skLineSegment(sketch, "E675", {"start": v(101.28, 81.54) * mm, "end": v(101.23, 81.47) * mm});
            skLineSegment(sketch, "E676", {"start": v(101.23, 81.47) * mm, "end": v(101.17, 81.4) * mm});
            skLineSegment(sketch, "E677", {"start": v(101.17, 81.4) * mm, "end": v(101.12, 81.34) * mm});
            skLineSegment(sketch, "E678", {"start": v(101.12, 81.34) * mm, "end": v(101.07, 81.27) * mm});
            skLineSegment(sketch, "E679", {"start": v(101.07, 81.27) * mm, "end": v(101.02, 81.2) * mm});
            skLineSegment(sketch, "E680", {"start": v(101.02, 81.2) * mm, "end": v(100.97, 81.12) * mm});
            skLineSegment(sketch, "E681", {"start": v(100.97, 81.12) * mm, "end": v(100.92, 81.04) * mm});
            skLineSegment(sketch, "E682", {"start": v(100.92, 81.04) * mm, "end": v(100.88, 80.96) * mm});
            skLineSegment(sketch, "E683", {"start": v(100.88, 80.96) * mm, "end": v(100.83, 80.88) * mm});
            skLineSegment(sketch, "E684", {"start": v(100.83, 80.88) * mm, "end": v(100.8, 80.8) * mm});
            skLineSegment(sketch, "E685", {"start": v(100.8, 80.8) * mm, "end": v(100.75, 80.71) * mm});
            skLineSegment(sketch, "E686", {"start": v(100.75, 80.71) * mm, "end": v(100.72, 80.62) * mm});
            skLineSegment(sketch, "E687", {"start": v(100.72, 80.62) * mm, "end": v(100.68, 80.54) * mm});
            skLineSegment(sketch, "E688", {"start": v(100.68, 80.54) * mm, "end": v(100.65, 80.44) * mm});
            skLineSegment(sketch, "E689", {"start": v(100.65, 80.44) * mm, "end": v(100.61, 80.35) * mm});
            skLineSegment(sketch, "E690", {"start": v(100.61, 80.35) * mm, "end": v(100.58, 80.26) * mm});
            skLineSegment(sketch, "E691", {"start": v(100.58, 80.26) * mm, "end": v(100.56, 80.16) * mm});
            skLineSegment(sketch, "E692", {"start": v(100.56, 80.16) * mm, "end": v(100.53, 80.06) * mm});
            skLineSegment(sketch, "E693", {"start": v(100.53, 80.06) * mm, "end": v(100.5, 79.97) * mm});
            skLineSegment(sketch, "E694", {"start": v(100.5, 79.97) * mm, "end": v(100.48, 79.87) * mm});
            skLineSegment(sketch, "E695", {"start": v(100.48, 79.87) * mm, "end": v(100.46, 79.76) * mm});
            skLineSegment(sketch, "E696", {"start": v(100.46, 79.76) * mm, "end": v(100.45, 79.66) * mm});
            skLineSegment(sketch, "E697", {"start": v(100.45, 79.66) * mm, "end": v(100.43, 79.56) * mm});
            skLineSegment(sketch, "E698", {"start": v(100.43, 79.56) * mm, "end": v(100.42, 79.45) * mm});
            skLineSegment(sketch, "E699", {"start": v(100.42, 79.45) * mm, "end": v(100.4, 79.35) * mm});
            skLineSegment(sketch, "E700", {"start": v(100.4, 79.35) * mm, "end": v(100.4, 79.24) * mm});
            skLineSegment(sketch, "E701", {"start": v(100.4, 79.24) * mm, "end": v(100.39, 79.13) * mm});
            skLineSegment(sketch, "E702", {"start": v(100.39, 79.13) * mm, "end": v(100.38, 79.02) * mm});
            skLineSegment(sketch, "E703", {"start": v(100.38, 79.02) * mm, "end": v(100.38, 78.92) * mm});
            skLineSegment(sketch, "E704", {"start": v(100.38, 78.92) * mm, "end": v(100.38, 78.8) * mm});
            skLineSegment(sketch, "E705", {"start": v(100.38, 78.8) * mm, "end": v(100.38, 78.7) * mm});
            skLineSegment(sketch, "E706", {"start": v(100.38, 78.7) * mm, "end": v(100.38, 78.58) * mm});
            skLineSegment(sketch, "E707", {"start": v(100.38, 78.58) * mm, "end": v(100.39, 78.47) * mm});
            skLineSegment(sketch, "E708", {"start": v(100.39, 78.47) * mm, "end": v(100.4, 78.36) * mm});
            skLineSegment(sketch, "E709", {"start": v(100.4, 78.36) * mm, "end": v(100.4, 78.25) * mm});
            skLineSegment(sketch, "E710", {"start": v(100.4, 78.25) * mm, "end": v(100.42, 78.14) * mm});
            skLineSegment(sketch, "E711", {"start": v(100.42, 78.14) * mm, "end": v(100.43, 78.02) * mm});
            skLineSegment(sketch, "E712", {"start": v(100.43, 78.02) * mm, "end": v(100.45, 77.91) * mm});
            skLineSegment(sketch, "E713", {"start": v(100.45, 77.91) * mm, "end": v(100.46, 77.8) * mm});
            skLineSegment(sketch, "E714", {"start": v(100.46, 77.8) * mm, "end": v(100.48, 77.69) * mm});
            skLineSegment(sketch, "E715", {"start": v(100.48, 77.69) * mm, "end": v(100.5, 77.58) * mm});
            skLineSegment(sketch, "E716", {"start": v(100.5, 77.58) * mm, "end": v(100.53, 77.46) * mm});
            skLineSegment(sketch, "E717", {"start": v(100.53, 77.46) * mm, "end": v(100.56, 77.35) * mm});
            skLineSegment(sketch, "E718", {"start": v(100.56, 77.35) * mm, "end": v(100.58, 77.24) * mm});
            skLineSegment(sketch, "E719", {"start": v(100.58, 77.24) * mm, "end": v(100.61, 77.13) * mm});
            skLineSegment(sketch, "E720", {"start": v(100.61, 77.13) * mm, "end": v(100.65, 77.02) * mm});
            skLineSegment(sketch, "E721", {"start": v(100.65, 77.02) * mm, "end": v(100.68, 76.91) * mm});
            skLineSegment(sketch, "E722", {"start": v(100.68, 76.91) * mm, "end": v(100.72, 76.8) * mm});
            skLineSegment(sketch, "E723", {"start": v(100.72, 76.8) * mm, "end": v(100.75, 76.7) * mm});
            skLineSegment(sketch, "E724", {"start": v(100.75, 76.7) * mm, "end": v(100.8, 76.6) * mm});
            skLineSegment(sketch, "E725", {"start": v(100.8, 76.6) * mm, "end": v(100.83, 76.49) * mm});
            skLineSegment(sketch, "E726", {"start": v(100.83, 76.49) * mm, "end": v(100.88, 76.38) * mm});
            skLineSegment(sketch, "E727", {"start": v(100.88, 76.38) * mm, "end": v(100.92, 76.28) * mm});
            skLineSegment(sketch, "E728", {"start": v(100.92, 76.28) * mm, "end": v(100.97, 76.18) * mm});
            skLineSegment(sketch, "E729", {"start": v(100.97, 76.18) * mm, "end": v(101.02, 76.07) * mm});
            skLineSegment(sketch, "E730", {"start": v(101.02, 76.07) * mm, "end": v(101.07, 75.97) * mm});
            skLineSegment(sketch, "E731", {"start": v(101.07, 75.97) * mm, "end": v(101.12, 75.88) * mm});
            skLineSegment(sketch, "E732", {"start": v(101.12, 75.88) * mm, "end": v(101.17, 75.78) * mm});
            skLineSegment(sketch, "E733", {"start": v(101.17, 75.78) * mm, "end": v(101.23, 75.68) * mm});
            skLineSegment(sketch, "E734", {"start": v(101.23, 75.68) * mm, "end": v(101.28, 75.59) * mm});
            skLineSegment(sketch, "E735", {"start": v(101.28, 75.59) * mm, "end": v(101.34, 75.5) * mm});
            skLineSegment(sketch, "E736", {"start": v(101.34, 75.5) * mm, "end": v(101.4, 75.4) * mm});
            skLineSegment(sketch, "E737", {"start": v(101.4, 75.4) * mm, "end": v(101.46, 75.32) * mm});
            skLineSegment(sketch, "E738", {"start": v(101.46, 75.32) * mm, "end": v(101.52, 75.23) * mm});
            skLineSegment(sketch, "E739", {"start": v(101.52, 75.23) * mm, "end": v(101.59, 75.14) * mm});
            skLineSegment(sketch, "E740", {"start": v(101.59, 75.14) * mm, "end": v(101.65, 75.06) * mm});
            skLineSegment(sketch, "E741", {"start": v(101.65, 75.06) * mm, "end": v(101.72, 74.98) * mm});
            skLineSegment(sketch, "E742", {"start": v(101.72, 74.98) * mm, "end": v(101.79, 74.9) * mm});
            skLineSegment(sketch, "E743", {"start": v(101.79, 74.9) * mm, "end": v(101.85, 74.82) * mm});
            skLineSegment(sketch, "E744", {"start": v(101.85, 74.82) * mm, "end": v(101.92, 74.75) * mm});
            skLineSegment(sketch, "E745", {"start": v(101.92, 74.75) * mm, "end": v(102, 74.68) * mm});
            skLineSegment(sketch, "E746", {"start": v(102, 74.68) * mm, "end": v(102.06, 74.6) * mm});
            skLineSegment(sketch, "E747", {"start": v(102.06, 74.6) * mm, "end": v(102.14, 74.54) * mm});
            skLineSegment(sketch, "E748", {"start": v(102.14, 74.54) * mm, "end": v(102.21, 74.47) * mm});
            skLineSegment(sketch, "E749", {"start": v(102.21, 74.47) * mm, "end": v(102.29, 74.4) * mm});
            skLineSegment(sketch, "E750", {"start": v(102.29, 74.4) * mm, "end": v(102.36, 74.35) * mm});
            skLineSegment(sketch, "E751", {"start": v(102.36, 74.35) * mm, "end": v(102.44, 74.29) * mm});
            skLineSegment(sketch, "E752", {"start": v(102.44, 74.29) * mm, "end": v(102.51, 74.23) * mm});
            skLineSegment(sketch, "E753", {"start": v(102.51, 74.23) * mm, "end": v(102.59, 74.18) * mm});
            skLineSegment(sketch, "E754", {"start": v(102.59, 74.18) * mm, "end": v(102.67, 74.13) * mm});
            skLineSegment(sketch, "E755", {"start": v(102.67, 74.13) * mm, "end": v(102.75, 74.08) * mm});
            skLineSegment(sketch, "E756", {"start": v(102.75, 74.08) * mm, "end": v(102.82, 74.04) * mm});
            skLineSegment(sketch, "E757", {"start": v(102.82, 74.04) * mm, "end": v(102.9, 74) * mm});
            skLineSegment(sketch, "E758", {"start": v(102.9, 74) * mm, "end": v(102.98, 73.95) * mm});
            skLineSegment(sketch, "E759", {"start": v(102.98, 73.95) * mm, "end": v(103.06, 73.92) * mm});
            skLineSegment(sketch, "E760", {"start": v(103.06, 73.92) * mm, "end": v(103.14, 73.88) * mm});
            skLineSegment(sketch, "E761", {"start": v(103.14, 73.88) * mm, "end": v(103.22, 73.85) * mm});
            skLineSegment(sketch, "E762", {"start": v(103.22, 73.85) * mm, "end": v(103.3, 73.82) * mm});
            skLineSegment(sketch, "E763", {"start": v(103.3, 73.82) * mm, "end": v(103.39, 73.8) * mm});
            skLineSegment(sketch, "E764", {"start": v(103.39, 73.8) * mm, "end": v(103.47, 73.77) * mm});
            skLineSegment(sketch, "E765", {"start": v(103.47, 73.77) * mm, "end": v(103.55, 73.75) * mm});
            skLineSegment(sketch, "E766", {"start": v(103.55, 73.75) * mm, "end": v(103.63, 73.73) * mm});
            skLineSegment(sketch, "E767", {"start": v(103.63, 73.73) * mm, "end": v(103.7, 73.72) * mm});
            skLineSegment(sketch, "E768", {"start": v(103.7, 73.72) * mm, "end": v(103.79, 73.7) * mm});
            skLineSegment(sketch, "E769", {"start": v(103.79, 73.7) * mm, "end": v(103.87, 73.7) * mm});
            skLineSegment(sketch, "E770", {"start": v(103.87, 73.7) * mm, "end": v(103.95, 73.7) * mm});
            skLineSegment(sketch, "E771", {"start": v(103.95, 73.7) * mm, "end": v(104.03, 73.7) * mm});
            skLineSegment(sketch, "E772", {"start": v(104.03, 73.7) * mm, "end": v(104.1, 73.7) * mm});
            skLineSegment(sketch, "E773", {"start": v(104.1, 73.7) * mm, "end": v(104.19, 73.7) * mm});
            skLineSegment(sketch, "E774", {"start": v(104.19, 73.7) * mm, "end": v(104.27, 73.7) * mm});
            skLineSegment(sketch, "E775", {"start": v(104.27, 73.7) * mm, "end": v(104.34, 73.71) * mm});
            skLineSegment(sketch, "E776", {"start": v(104.34, 73.71) * mm, "end": v(104.42, 73.72) * mm});
            skLineSegment(sketch, "E777", {"start": v(104.42, 73.72) * mm, "end": v(104.5, 73.74) * mm});
            skLineSegment(sketch, "E778", {"start": v(104.5, 73.74) * mm, "end": v(104.57, 73.76) * mm});
            skLineSegment(sketch, "E779", {"start": v(104.57, 73.76) * mm, "end": v(104.65, 73.78) * mm});
            skLineSegment(sketch, "E780", {"start": v(104.65, 73.78) * mm, "end": v(104.72, 73.8) * mm});
            skLineSegment(sketch, "E781", {"start": v(104.72, 73.8) * mm, "end": v(104.8, 73.83) * mm});
            skLineSegment(sketch, "E782", {"start": v(104.8, 73.83) * mm, "end": v(104.87, 73.86) * mm});
            skLineSegment(sketch, "E783", {"start": v(104.87, 73.86) * mm, "end": v(104.94, 73.89) * mm});
            skLineSegment(sketch, "E784", {"start": v(104.94, 73.89) * mm, "end": v(105, 73.92) * mm});
            skLineSegment(sketch, "E785", {"start": v(105, 73.92) * mm, "end": v(105.08, 73.96) * mm});
            skLineSegment(sketch, "E786", {"start": v(105.08, 73.96) * mm, "end": v(105.15, 74) * mm});
            skLineSegment(sketch, "E787", {"start": v(105.15, 74) * mm, "end": v(105.21, 74.04) * mm});
            skLineSegment(sketch, "E788", {"start": v(105.21, 74.04) * mm, "end": v(105.28, 74.09) * mm});
            skLineSegment(sketch, "E789", {"start": v(105.28, 74.09) * mm, "end": v(105.35, 74.14) * mm});
            skLineSegment(sketch, "E790", {"start": v(105.35, 74.14) * mm, "end": v(105.4, 74.19) * mm});
            skLineSegment(sketch, "E791", {"start": v(105.4, 74.19) * mm, "end": v(105.47, 74.24) * mm});
            skLineSegment(sketch, "E792", {"start": v(105.47, 74.24) * mm, "end": v(105.53, 74.3) * mm});
            skLineSegment(sketch, "E793", {"start": v(105.53, 74.3) * mm, "end": v(105.6, 74.36) * mm});
            skLineSegment(sketch, "E794", {"start": v(105.6, 74.36) * mm, "end": v(105.65, 74.42) * mm});
            skLineSegment(sketch, "E795", {"start": v(105.65, 74.42) * mm, "end": v(105.7, 74.48) * mm});
            skLineSegment(sketch, "E796", {"start": v(105.7, 74.48) * mm, "end": v(105.76, 74.55) * mm});
            skLineSegment(sketch, "E797", {"start": v(105.76, 74.55) * mm, "end": v(105.81, 74.62) * mm});
            skLineSegment(sketch, "E798", {"start": v(105.81, 74.62) * mm, "end": v(105.87, 74.69) * mm});
            skLineSegment(sketch, "E799", {"start": v(105.87, 74.69) * mm, "end": v(105.92, 74.76) * mm});
            skLineSegment(sketch, "E800", {"start": v(105.92, 74.76) * mm, "end": v(105.96, 74.84) * mm});
            skLineSegment(sketch, "E801", {"start": v(105.96, 74.84) * mm, "end": v(106.01, 74.91) * mm});
            skLineSegment(sketch, "E802", {"start": v(106.01, 74.91) * mm, "end": v(106.06, 75) * mm});
            skLineSegment(sketch, "E803", {"start": v(106.06, 75) * mm, "end": v(106.1, 75.08) * mm});
            skLineSegment(sketch, "E804", {"start": v(106.1, 75.08) * mm, "end": v(106.14, 75.16) * mm});
            skLineSegment(sketch, "E805", {"start": v(106.14, 75.16) * mm, "end": v(106.18, 75.24) * mm});
            skLineSegment(sketch, "E806", {"start": v(106.18, 75.24) * mm, "end": v(106.22, 75.33) * mm});
            skLineSegment(sketch, "E807", {"start": v(106.22, 75.33) * mm, "end": v(106.25, 75.42) * mm});
            skLineSegment(sketch, "E808", {"start": v(106.25, 75.42) * mm, "end": v(106.29, 75.51) * mm});
            skLineSegment(sketch, "E809", {"start": v(106.29, 75.51) * mm, "end": v(106.32, 75.6) * mm});
            skLineSegment(sketch, "E810", {"start": v(106.32, 75.6) * mm, "end": v(106.35, 75.7) * mm});
            skLineSegment(sketch, "E811", {"start": v(106.35, 75.7) * mm, "end": v(106.38, 75.8) * mm});
            skLineSegment(sketch, "E812", {"start": v(106.38, 75.8) * mm, "end": v(106.4, 75.9) * mm});
            skLineSegment(sketch, "E813", {"start": v(106.4, 75.9) * mm, "end": v(106.43, 76) * mm});
            skLineSegment(sketch, "E814", {"start": v(106.43, 76) * mm, "end": v(106.45, 76.1) * mm});
            skLineSegment(sketch, "E815", {"start": v(106.45, 76.1) * mm, "end": v(106.47, 76.2) * mm});
            skLineSegment(sketch, "E816", {"start": v(106.47, 76.2) * mm, "end": v(106.49, 76.3) * mm});
            skLineSegment(sketch, "E817", {"start": v(106.49, 76.3) * mm, "end": v(106.5, 76.4) * mm});
            skLineSegment(sketch, "E818", {"start": v(106.5, 76.4) * mm, "end": v(106.52, 76.5) * mm});
            skLineSegment(sketch, "E819", {"start": v(106.52, 76.5) * mm, "end": v(106.53, 76.6) * mm});
            skLineSegment(sketch, "E820", {"start": v(106.53, 76.6) * mm, "end": v(106.54, 76.72) * mm});
            skLineSegment(sketch, "E821", {"start": v(106.54, 76.72) * mm, "end": v(106.54, 76.82) * mm});
            skLineSegment(sketch, "E822", {"start": v(106.54, 76.82) * mm, "end": v(106.55, 76.93) * mm});
            skLineSegment(sketch, "E823", {"start": v(106.55, 76.93) * mm, "end": v(106.55, 77.04) * mm});
            skLineSegment(sketch, "E824", {"start": v(106.55, 77.04) * mm, "end": v(106.55, 77.13) * mm});
            skArc(sketch, "E825", {"start": v(104.16, 81.9) * mm, "mid": v(103.8, 78.07) * mm, "end": v(106.02, 74.93) * mm});
            skLineSegment(sketch, "E826", {"start": v(112.73, 60.8) * mm, "end": v(109.36, 59.9) * mm});
            skLineSegment(sketch, "E827", {"start": v(112.73, 60.8) * mm, "end": v(112.94, 61.25) * mm});
            skLineSegment(sketch, "E828", {"start": v(104.14, 97.57) * mm, "end": v(100.78, 96.67) * mm});
            skLineSegment(sketch, "E829", {"start": v(104.23, 96.97) * mm, "end": v(104.14, 97.57) * mm});
            skLineSegment(sketch, "E830", {"start": v(111.1, 60.32) * mm, "end": v(107.73, 59.42) * mm});
            skLineSegment(sketch, "E831", {"start": v(111.1, 60.32) * mm, "end": v(111.14, 60.38) * mm});
            skArc(sketch, "E832", {"start": v(103.62, 79.7) * mm, "mid": v(103.84, 78.08) * mm, "end": v(104.46, 76.57) * mm});
            skLineSegment(sketch, "E833", {"start": v(102.44, 97.4) * mm, "end": v(99.07, 96.5) * mm});
            skLineSegment(sketch, "E834", {"start": v(102.5, 97.13) * mm, "end": v(102.44, 97.4) * mm});
            skLineSegment(sketch, "E835", {"start": v(107.67, 59.7) * mm, "end": v(106.03, 59.26) * mm});
            skLineSegment(sketch, "E836", {"start": v(99.04, 96.44) * mm, "end": v(97.45, 96.02) * mm});
            skLineSegment(sketch, "E837", {"start": v(105.95, 59.86) * mm, "end": v(104.29, 59.41) * mm});
            skLineSegment(sketch, "E838", {"start": v(97.24, 95.58) * mm, "end": v(95.92, 95.23) * mm});
            skLineSegment(sketch, "E839", {"start": v(104.24, 60.34) * mm, "end": v(102.52, 59.88) * mm});
            skLineSegment(sketch, "E840", {"start": v(95.66, 94.45) * mm, "end": v(94.52, 94.14) * mm});
            skLineSegment(sketch, "E841", {"start": v(102.59, 61.15) * mm, "end": v(100.78, 60.66) * mm});
            skLineSegment(sketch, "E842", {"start": v(94.3, 93.05) * mm, "end": v(93.28, 92.78) * mm});
            skLineSegment(sketch, "E843", {"start": v(93.14, 91.4) * mm, "end": v(92.2, 91.16) * mm});
            skLineSegment(sketch, "E844", {"start": v(92.2, 89.55) * mm, "end": v(91.32, 89.32) * mm});
            skLineSegment(sketch, "E845", {"start": v(91.5, 87.5) * mm, "end": v(90.65, 87.28) * mm});
            skLineSegment(sketch, "E846", {"start": v(91.02, 85.3) * mm, "end": v(90.2, 85.08) * mm});
            skLineSegment(sketch, "E847", {"start": v(90.78, 82.98) * mm, "end": v(89.96, 82.76) * mm});
            skLineSegment(sketch, "E848", {"start": v(90.8, 80.58) * mm, "end": v(89.96, 80.36) * mm});
            skLineSegment(sketch, "E849", {"start": v(91.05, 78.15) * mm, "end": v(90.2, 77.92) * mm});
            skLineSegment(sketch, "E850", {"start": v(91.54, 75.72) * mm, "end": v(90.65, 75.48) * mm});
            skSolve(sketch);
        }
        {
            var Q0;
            Q0=makeQuery(id+"F0.imprint","IMPRINT",FACE,{"disambiguationData":[TD([[makeQuery(id+"F0.imprint","IMPRINT",EDGE,{"derivedFrom":sQuery(id+"F0.wireOp",EDGE,"E11")}),1.0]])]});
            extrude(context, id + "F1", {"entities" : qUnion([Q0]), "depth" : 9.52 * mm, "offsetDistance" : 25.4 * mm});
        }
        {
            var Q0;
            Q0=makeQuery(id+"F1.opExtrude","CAP_FACE",FACE,{"disambiguationData":[OSD([sQuery(id+"F0.wireOp",EDGE,"E11"),sQuery(id+"F0.wireOp",EDGE,"E12"),sQuery(id+"F0.wireOp",EDGE,"E13"),sQuery(id+"F0.wireOp",EDGE,"E14"),sQuery(id+"F0.wireOp",EDGE,"E15"),sQuery(id+"F0.wireOp",EDGE,"E16"),sQuery(id+"F0.wireOp",EDGE,"E17"),sQuery(id+"F0.wireOp",EDGE,"E18"),sQuery(id+"F0.wireOp",EDGE,"E19"),sQuery(id+"F0.wireOp",EDGE,"E20"),sQuery(id+"F0.wireOp",EDGE,"E21"),sQuery(id+"F0.wireOp",EDGE,"E22"),sQuery(id+"F0.wireOp",EDGE,"E23"),sQuery(id+"F0.wireOp",EDGE,"E24"),sQuery(id+"F0.wireOp",EDGE,"E25"),sQuery(id+"F0.wireOp",EDGE,"E26"),sQuery(id+"F0.wireOp",EDGE,"E27"),sQuery(id+"F0.wireOp",EDGE,"E28"),sQuery(id+"F0.wireOp",EDGE,"E29"),sQuery(id+"F0.wireOp",EDGE,"E30"),sQuery(id+"F0.wireOp",EDGE,"E31"),sQuery(id+"F0.wireOp",EDGE,"E32"),sQuery(id+"F0.wireOp",EDGE,"E33"),sQuery(id+"F0.wireOp",EDGE,"E34"),sQuery(id+"F0.wireOp",EDGE,"E35"),sQuery(id+"F0.wireOp",EDGE,"E36"),sQuery(id+"F0.wireOp",EDGE,"E37"),sQuery(id+"F0.wireOp",EDGE,"E38"),sQuery(id+"F0.wireOp",EDGE,"E39"),sQuery(id+"F0.wireOp",EDGE,"E40"),sQuery(id+"F0.wireOp",EDGE,"E41"),sQuery(id+"F0.wireOp",EDGE,"E42"),sQuery(id+"F0.wireOp",EDGE,"E43"),sQuery(id+"F0.wireOp",EDGE,"E44"),sQuery(id+"F0.wireOp",EDGE,"E45"),sQuery(id+"F0.wireOp",EDGE,"E46"),sQuery(id+"F0.wireOp",EDGE,"E47"),sQuery(id+"F0.wireOp",EDGE,"E48"),sQuery(id+"F0.wireOp",EDGE,"E49"),sQuery(id+"F0.wireOp",EDGE,"E50"),sQuery(id+"F0.wireOp",EDGE,"E51"),sQuery(id+"F0.wireOp",EDGE,"E52"),sQuery(id+"F0.wireOp",EDGE,"E53"),sQuery(id+"F0.wireOp",EDGE,"E54"),sQuery(id+"F0.wireOp",EDGE,"E55"),sQuery(id+"F0.wireOp",EDGE,"E56"),sQuery(id+"F0.wireOp",EDGE,"E57"),sQuery(id+"F0.wireOp",EDGE,"E58"),sQuery(id+"F0.wireOp",EDGE,"E59"),sQuery(id+"F0.wireOp",EDGE,"E60"),sQuery(id+"F0.wireOp",EDGE,"E61"),sQuery(id+"F0.wireOp",EDGE,"E62"),sQuery(id+"F0.wireOp",EDGE,"E63"),sQuery(id+"F0.wireOp",EDGE,"E64"),sQuery(id+"F0.wireOp",EDGE,"E65"),sQuery(id+"F0.wireOp",EDGE,"E66"),sQuery(id+"F0.wireOp",EDGE,"E67"),sQuery(id+"F0.wireOp",EDGE,"E68"),sQuery(id+"F0.wireOp",EDGE,"E69"),sQuery(id+"F0.wireOp",EDGE,"E70"),sQuery(id+"F0.wireOp",EDGE,"E71"),sQuery(id+"F0.wireOp",EDGE,"E72"),sQuery(id+"F0.wireOp",EDGE,"E73"),sQuery(id+"F0.wireOp",EDGE,"E74"),sQuery(id+"F0.wireOp",EDGE,"E75"),sQuery(id+"F0.wireOp",EDGE,"E76"),sQuery(id+"F0.wireOp",EDGE,"E77"),sQuery(id+"F0.wireOp",EDGE,"E78"),sQuery(id+"F0.wireOp",EDGE,"E79"),sQuery(id+"F0.wireOp",EDGE,"E80"),sQuery(id+"F0.wireOp",EDGE,"E81"),sQuery(id+"F0.wireOp",EDGE,"E82"),sQuery(id+"F0.wireOp",EDGE,"E83"),sQuery(id+"F0.wireOp",EDGE,"E84"),sQuery(id+"F0.wireOp",EDGE,"E85"),sQuery(id+"F0.wireOp",EDGE,"E86"),sQuery(id+"F0.wireOp",EDGE,"E87"),sQuery(id+"F0.wireOp",EDGE,"E88"),sQuery(id+"F0.wireOp",EDGE,"E89"),sQuery(id+"F0.wireOp",EDGE,"E90"),sQuery(id+"F0.wireOp",EDGE,"E91"),sQuery(id+"F0.wireOp",EDGE,"E92"),sQuery(id+"F0.wireOp",EDGE,"E93"),sQuery(id+"F0.wireOp",EDGE,"E94"),sQuery(id+"F0.wireOp",EDGE,"E95"),sQuery(id+"F0.wireOp",EDGE,"E96"),sQuery(id+"F0.wireOp",EDGE,"E97"),sQuery(id+"F0.wireOp",EDGE,"E98"),sQuery(id+"F0.wireOp",EDGE,"E99"),sQuery(id+"F0.wireOp",EDGE,"E100"),sQuery(id+"F0.wireOp",EDGE,"E101"),sQuery(id+"F0.wireOp",EDGE,"E102"),sQuery(id+"F0.wireOp",EDGE,"E103"),sQuery(id+"F0.wireOp",EDGE,"E104"),sQuery(id+"F0.wireOp",EDGE,"E105"),sQuery(id+"F0.wireOp",EDGE,"E106"),sQuery(id+"F0.wireOp",EDGE,"E107")])],"isStart":false});
            var sketch = newSketch(context, id + "F2", { "sketchPlane" : qUnion([Q0])});
            skCircle(sketch, "E851", {"center": v(-55.95, -6.6) * mm, "radius": 12.95 * mm});
            skSolve(sketch);
        }
        {
            var Q0;
            Q0=makeQuery(id+"F2.imprint","IMPRINT",FACE,{"disambiguationData":[TD([[makeQuery(id+"F2.imprint","IMPRINT",EDGE,{"derivedFrom":sQuery(id+"F2.wireOp",EDGE,"E851")}),1.0]])]});
            extrude(context, id + "F3", {"entities" : qUnion([Q0]), "operationType" : NewBodyOperationType.REMOVE, "oppositeDirection" : true, "depth" : 34.3 * mm, "offsetDistance" : 25.4 * mm});
        }
    });
